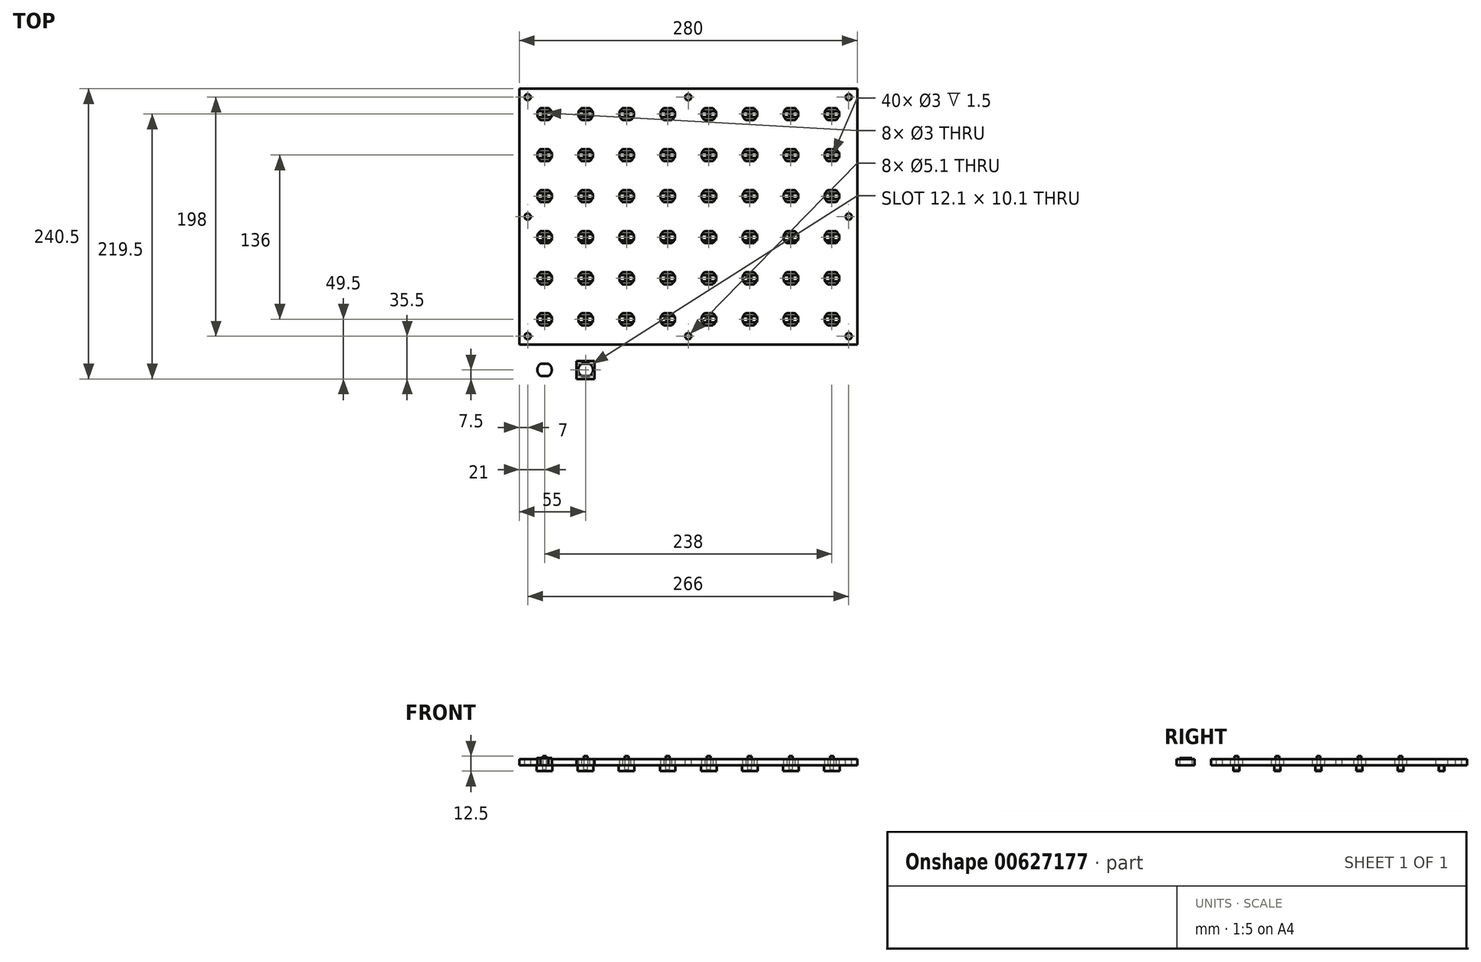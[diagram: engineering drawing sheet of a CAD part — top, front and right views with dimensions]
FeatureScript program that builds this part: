
annotation { "Feature Type Name" : "Feature", "Feature Type Description" : "" }
export const myFeature = defineFeature(function(context is Context, id is Id, definition is map)
    precondition{}
    {
        {
            var Q0;
            Q0=qCreatedBy(makeId("Top.planeOp"),FACE);
            var sketch = newSketch(context, id + "F0", { "sketchPlane" : qUnion([Q0])});
            skLineSegment(sketch, "E0.bottom", {"start": v(-140, -106) * mm, "end": v(140, -106) * mm});
            skLineSegment(sketch, "E0.top", {"start": v(-140, 106) * mm, "end": v(140, 106) * mm});
            skLineSegment(sketch, "E0.left", {"start": v(-140, -106) * mm, "end": v(-140, 106) * mm});
            skLineSegment(sketch, "E0.right", {"start": v(140, -106) * mm, "end": v(140, 106) * mm});
            skPoint(sketch, "E0.middle", {"position": v(0, 0) * mm});
            skLineSegment(sketch, "E1", {"start": v(-102, 141.86) * mm, "end": v(-102, -178.14) * mm, "construction": true});
            skLineSegment(sketch, "E2", {"start": v(-122.32, -80) * mm, "end": v(-115.68, -80) * mm});
            skLineSegment(sketch, "E3", {"start": v(-122.32, -90) * mm, "end": v(-115.68, -90) * mm});
            skArc(sketch, "E4", {"start": v(-122.32, -80) * mm, "mid": v(-125, -85) * mm, "end": v(-122.32, -90) * mm});
            skArc(sketch, "E5", {"start": v(-115.68, -90) * mm, "mid": v(-113, -85) * mm, "end": v(-115.68, -80) * mm});
            skLineSegment(sketch, "E6", {"start": v(-165.76, -85) * mm, "end": v(184.24, -85) * mm, "construction": true});
            skLineSegment(sketch, "E7.0.1.0", {"start": v(-165.76, -51) * mm, "end": v(184.24, -51) * mm, "construction": true});
            skArc(sketch, "E7.0.1.1", {"start": v(-122.32, -46) * mm, "mid": v(-125, -51) * mm, "end": v(-122.32, -56) * mm});
            skLineSegment(sketch, "E7.0.1.2", {"start": v(-122.32, -56) * mm, "end": v(-115.68, -56) * mm});
            skLineSegment(sketch, "E7.0.1.3", {"start": v(-122.32, -46) * mm, "end": v(-115.68, -46) * mm});
            skArc(sketch, "E7.0.1.4", {"start": v(-115.68, -56) * mm, "mid": v(-113, -51) * mm, "end": v(-115.68, -46) * mm});
            skLineSegment(sketch, "E7.0.2.0", {"start": v(-165.76, -17) * mm, "end": v(184.24, -17) * mm, "construction": true});
            skArc(sketch, "E7.0.2.1", {"start": v(-122.32, -12) * mm, "mid": v(-125, -17) * mm, "end": v(-122.32, -22) * mm});
            skLineSegment(sketch, "E7.0.2.2", {"start": v(-122.32, -22) * mm, "end": v(-115.68, -22) * mm});
            skLineSegment(sketch, "E7.0.2.3", {"start": v(-122.32, -12) * mm, "end": v(-115.68, -12) * mm});
            skArc(sketch, "E7.0.2.4", {"start": v(-115.68, -22) * mm, "mid": v(-113, -17) * mm, "end": v(-115.68, -12) * mm});
            skLineSegment(sketch, "E7.0.3.0", {"start": v(-165.76, 17) * mm, "end": v(184.24, 17) * mm, "construction": true});
            skArc(sketch, "E7.0.3.1", {"start": v(-122.32, 22) * mm, "mid": v(-125, 17) * mm, "end": v(-122.32, 12) * mm});
            skLineSegment(sketch, "E7.0.3.2", {"start": v(-122.32, 12) * mm, "end": v(-115.68, 12) * mm});
            skLineSegment(sketch, "E7.0.3.3", {"start": v(-122.32, 22) * mm, "end": v(-115.68, 22) * mm});
            skArc(sketch, "E7.0.3.4", {"start": v(-115.68, 12) * mm, "mid": v(-113, 17) * mm, "end": v(-115.68, 22) * mm});
            skLineSegment(sketch, "E7.0.4.0", {"start": v(-165.76, 51) * mm, "end": v(184.24, 51) * mm, "construction": true});
            skArc(sketch, "E7.0.4.1", {"start": v(-122.32, 56) * mm, "mid": v(-125, 51) * mm, "end": v(-122.32, 46) * mm});
            skLineSegment(sketch, "E7.0.4.2", {"start": v(-122.32, 46) * mm, "end": v(-115.68, 46) * mm});
            skLineSegment(sketch, "E7.0.4.3", {"start": v(-122.32, 56) * mm, "end": v(-115.68, 56) * mm});
            skArc(sketch, "E7.0.4.4", {"start": v(-115.68, 46) * mm, "mid": v(-113, 51) * mm, "end": v(-115.68, 56) * mm});
            skLineSegment(sketch, "E7.1.0.0", {"start": v(-131.76, -85) * mm, "end": v(218.24, -85) * mm, "construction": true});
            skArc(sketch, "E7.1.0.1", {"start": v(-88.32, -80) * mm, "mid": v(-91, -85) * mm, "end": v(-88.32, -90) * mm});
            skLineSegment(sketch, "E7.1.0.2", {"start": v(-88.32, -90) * mm, "end": v(-81.68, -90) * mm});
            skLineSegment(sketch, "E7.1.0.3", {"start": v(-88.32, -80) * mm, "end": v(-81.68, -80) * mm});
            skArc(sketch, "E7.1.0.4", {"start": v(-81.68, -90) * mm, "mid": v(-79, -85) * mm, "end": v(-81.68, -80) * mm});
            skLineSegment(sketch, "E7.1.1.0", {"start": v(-131.76, -51) * mm, "end": v(218.24, -51) * mm, "construction": true});
            skArc(sketch, "E7.1.1.1", {"start": v(-88.32, -46) * mm, "mid": v(-91, -51) * mm, "end": v(-88.32, -56) * mm});
            skLineSegment(sketch, "E7.1.1.2", {"start": v(-88.32, -56) * mm, "end": v(-81.68, -56) * mm});
            skLineSegment(sketch, "E7.1.1.3", {"start": v(-88.32, -46) * mm, "end": v(-81.68, -46) * mm});
            skArc(sketch, "E7.1.1.4", {"start": v(-81.68, -56) * mm, "mid": v(-79, -51) * mm, "end": v(-81.68, -46) * mm});
            skLineSegment(sketch, "E7.1.2.0", {"start": v(-131.76, -17) * mm, "end": v(218.24, -17) * mm, "construction": true});
            skArc(sketch, "E7.1.2.1", {"start": v(-88.32, -12) * mm, "mid": v(-91, -17) * mm, "end": v(-88.32, -22) * mm});
            skLineSegment(sketch, "E7.1.2.2", {"start": v(-88.32, -22) * mm, "end": v(-81.68, -22) * mm});
            skLineSegment(sketch, "E7.1.2.3", {"start": v(-88.32, -12) * mm, "end": v(-81.68, -12) * mm});
            skArc(sketch, "E7.1.2.4", {"start": v(-81.68, -22) * mm, "mid": v(-79, -17) * mm, "end": v(-81.68, -12) * mm});
            skLineSegment(sketch, "E7.1.3.0", {"start": v(-131.76, 17) * mm, "end": v(218.24, 17) * mm, "construction": true});
            skArc(sketch, "E7.1.3.1", {"start": v(-88.32, 22) * mm, "mid": v(-91, 17) * mm, "end": v(-88.32, 12) * mm});
            skLineSegment(sketch, "E7.1.3.2", {"start": v(-88.32, 12) * mm, "end": v(-81.68, 12) * mm});
            skLineSegment(sketch, "E7.1.3.3", {"start": v(-88.32, 22) * mm, "end": v(-81.68, 22) * mm});
            skArc(sketch, "E7.1.3.4", {"start": v(-81.68, 12) * mm, "mid": v(-79, 17) * mm, "end": v(-81.68, 22) * mm});
            skLineSegment(sketch, "E7.1.4.0", {"start": v(-131.76, 51) * mm, "end": v(218.24, 51) * mm, "construction": true});
            skArc(sketch, "E7.1.4.1", {"start": v(-88.32, 56) * mm, "mid": v(-91, 51) * mm, "end": v(-88.32, 46) * mm});
            skLineSegment(sketch, "E7.1.4.2", {"start": v(-88.32, 46) * mm, "end": v(-81.68, 46) * mm});
            skLineSegment(sketch, "E7.1.4.3", {"start": v(-88.32, 56) * mm, "end": v(-81.68, 56) * mm});
            skArc(sketch, "E7.1.4.4", {"start": v(-81.68, 46) * mm, "mid": v(-79, 51) * mm, "end": v(-81.68, 56) * mm});
            skLineSegment(sketch, "E7.2.0.0", {"start": v(-97.76, -85) * mm, "end": v(252.24, -85) * mm, "construction": true});
            skArc(sketch, "E7.2.0.1", {"start": v(-54.32, -80) * mm, "mid": v(-57, -85) * mm, "end": v(-54.32, -90) * mm});
            skLineSegment(sketch, "E7.2.0.2", {"start": v(-54.32, -90) * mm, "end": v(-47.68, -90) * mm});
            skLineSegment(sketch, "E7.2.0.3", {"start": v(-54.32, -80) * mm, "end": v(-47.68, -80) * mm});
            skArc(sketch, "E7.2.0.4", {"start": v(-47.68, -90) * mm, "mid": v(-45, -85) * mm, "end": v(-47.68, -80) * mm});
            skLineSegment(sketch, "E7.2.1.0", {"start": v(-97.76, -51) * mm, "end": v(252.24, -51) * mm, "construction": true});
            skArc(sketch, "E7.2.1.1", {"start": v(-54.32, -46) * mm, "mid": v(-57, -51) * mm, "end": v(-54.32, -56) * mm});
            skLineSegment(sketch, "E7.2.1.2", {"start": v(-54.32, -56) * mm, "end": v(-47.68, -56) * mm});
            skLineSegment(sketch, "E7.2.1.3", {"start": v(-54.32, -46) * mm, "end": v(-47.68, -46) * mm});
            skArc(sketch, "E7.2.1.4", {"start": v(-47.68, -56) * mm, "mid": v(-45, -51) * mm, "end": v(-47.68, -46) * mm});
            skLineSegment(sketch, "E7.2.2.0", {"start": v(-97.76, -17) * mm, "end": v(252.24, -17) * mm, "construction": true});
            skArc(sketch, "E7.2.2.1", {"start": v(-54.32, -12) * mm, "mid": v(-57, -17) * mm, "end": v(-54.32, -22) * mm});
            skLineSegment(sketch, "E7.2.2.2", {"start": v(-54.32, -22) * mm, "end": v(-47.68, -22) * mm});
            skLineSegment(sketch, "E7.2.2.3", {"start": v(-54.32, -12) * mm, "end": v(-47.68, -12) * mm});
            skArc(sketch, "E7.2.2.4", {"start": v(-47.68, -22) * mm, "mid": v(-45, -17) * mm, "end": v(-47.68, -12) * mm});
            skLineSegment(sketch, "E7.2.3.0", {"start": v(-97.76, 17) * mm, "end": v(252.24, 17) * mm, "construction": true});
            skArc(sketch, "E7.2.3.1", {"start": v(-54.32, 22) * mm, "mid": v(-57, 17) * mm, "end": v(-54.32, 12) * mm});
            skLineSegment(sketch, "E7.2.3.2", {"start": v(-54.32, 12) * mm, "end": v(-47.68, 12) * mm});
            skLineSegment(sketch, "E7.2.3.3", {"start": v(-54.32, 22) * mm, "end": v(-47.68, 22) * mm});
            skArc(sketch, "E7.2.3.4", {"start": v(-47.68, 12) * mm, "mid": v(-45, 17) * mm, "end": v(-47.68, 22) * mm});
            skLineSegment(sketch, "E7.2.4.0", {"start": v(-97.76, 51) * mm, "end": v(252.24, 51) * mm, "construction": true});
            skArc(sketch, "E7.2.4.1", {"start": v(-54.32, 56) * mm, "mid": v(-57, 51) * mm, "end": v(-54.32, 46) * mm});
            skLineSegment(sketch, "E7.2.4.2", {"start": v(-54.32, 46) * mm, "end": v(-47.68, 46) * mm});
            skLineSegment(sketch, "E7.2.4.3", {"start": v(-54.32, 56) * mm, "end": v(-47.68, 56) * mm});
            skArc(sketch, "E7.2.4.4", {"start": v(-47.68, 46) * mm, "mid": v(-45, 51) * mm, "end": v(-47.68, 56) * mm});
            skLineSegment(sketch, "E7.3.0.0", {"start": v(-63.76, -85) * mm, "end": v(286.24, -85) * mm, "construction": true});
            skArc(sketch, "E7.3.0.1", {"start": v(-20.32, -80) * mm, "mid": v(-23, -85) * mm, "end": v(-20.32, -90) * mm});
            skLineSegment(sketch, "E7.3.0.2", {"start": v(-20.32, -90) * mm, "end": v(-13.68, -90) * mm});
            skLineSegment(sketch, "E7.3.0.3", {"start": v(-20.32, -80) * mm, "end": v(-13.68, -80) * mm});
            skArc(sketch, "E7.3.0.4", {"start": v(-13.68, -90) * mm, "mid": v(-11, -85) * mm, "end": v(-13.68, -80) * mm});
            skLineSegment(sketch, "E7.3.1.0", {"start": v(-63.76, -51) * mm, "end": v(286.24, -51) * mm, "construction": true});
            skArc(sketch, "E7.3.1.1", {"start": v(-20.32, -46) * mm, "mid": v(-23, -51) * mm, "end": v(-20.32, -56) * mm});
            skLineSegment(sketch, "E7.3.1.2", {"start": v(-20.32, -56) * mm, "end": v(-13.68, -56) * mm});
            skLineSegment(sketch, "E7.3.1.3", {"start": v(-20.32, -46) * mm, "end": v(-13.68, -46) * mm});
            skArc(sketch, "E7.3.1.4", {"start": v(-13.68, -56) * mm, "mid": v(-11, -51) * mm, "end": v(-13.68, -46) * mm});
            skLineSegment(sketch, "E7.3.2.0", {"start": v(-63.76, -17) * mm, "end": v(286.24, -17) * mm, "construction": true});
            skArc(sketch, "E7.3.2.1", {"start": v(-20.32, -12) * mm, "mid": v(-23, -17) * mm, "end": v(-20.32, -22) * mm});
            skLineSegment(sketch, "E7.3.2.2", {"start": v(-20.32, -22) * mm, "end": v(-13.68, -22) * mm});
            skLineSegment(sketch, "E7.3.2.3", {"start": v(-20.32, -12) * mm, "end": v(-13.68, -12) * mm});
            skArc(sketch, "E7.3.2.4", {"start": v(-13.68, -22) * mm, "mid": v(-11, -17) * mm, "end": v(-13.68, -12) * mm});
            skLineSegment(sketch, "E7.3.3.0", {"start": v(-63.76, 17) * mm, "end": v(286.24, 17) * mm, "construction": true});
            skArc(sketch, "E7.3.3.1", {"start": v(-20.32, 22) * mm, "mid": v(-23, 17) * mm, "end": v(-20.32, 12) * mm});
            skLineSegment(sketch, "E7.3.3.2", {"start": v(-20.32, 12) * mm, "end": v(-13.68, 12) * mm});
            skLineSegment(sketch, "E7.3.3.3", {"start": v(-20.32, 22) * mm, "end": v(-13.68, 22) * mm});
            skArc(sketch, "E7.3.3.4", {"start": v(-13.68, 12) * mm, "mid": v(-11, 17) * mm, "end": v(-13.68, 22) * mm});
            skLineSegment(sketch, "E7.3.4.0", {"start": v(-63.76, 51) * mm, "end": v(286.24, 51) * mm, "construction": true});
            skArc(sketch, "E7.3.4.1", {"start": v(-20.32, 56) * mm, "mid": v(-23, 51) * mm, "end": v(-20.32, 46) * mm});
            skLineSegment(sketch, "E7.3.4.2", {"start": v(-20.32, 46) * mm, "end": v(-13.68, 46) * mm});
            skLineSegment(sketch, "E7.3.4.3", {"start": v(-20.32, 56) * mm, "end": v(-13.68, 56) * mm});
            skArc(sketch, "E7.3.4.4", {"start": v(-13.68, 46) * mm, "mid": v(-11, 51) * mm, "end": v(-13.68, 56) * mm});
            skLineSegment(sketch, "E7.4.0.0", {"start": v(-29.76, -85) * mm, "end": v(320.24, -85) * mm, "construction": true});
            skArc(sketch, "E7.4.0.1", {"start": v(13.68, -80) * mm, "mid": v(11, -85) * mm, "end": v(13.68, -90) * mm});
            skLineSegment(sketch, "E7.4.0.2", {"start": v(13.68, -90) * mm, "end": v(20.32, -90) * mm});
            skLineSegment(sketch, "E7.4.0.3", {"start": v(13.68, -80) * mm, "end": v(20.32, -80) * mm});
            skArc(sketch, "E7.4.0.4", {"start": v(20.32, -90) * mm, "mid": v(23, -85) * mm, "end": v(20.32, -80) * mm});
            skLineSegment(sketch, "E7.4.1.0", {"start": v(-29.76, -51) * mm, "end": v(320.24, -51) * mm, "construction": true});
            skArc(sketch, "E7.4.1.1", {"start": v(13.68, -46) * mm, "mid": v(11, -51) * mm, "end": v(13.68, -56) * mm});
            skLineSegment(sketch, "E7.4.1.2", {"start": v(13.68, -56) * mm, "end": v(20.32, -56) * mm});
            skLineSegment(sketch, "E7.4.1.3", {"start": v(13.68, -46) * mm, "end": v(20.32, -46) * mm});
            skArc(sketch, "E7.4.1.4", {"start": v(20.32, -56) * mm, "mid": v(23, -51) * mm, "end": v(20.32, -46) * mm});
            skLineSegment(sketch, "E7.4.2.0", {"start": v(-29.76, -17) * mm, "end": v(320.24, -17) * mm, "construction": true});
            skArc(sketch, "E7.4.2.1", {"start": v(13.68, -12) * mm, "mid": v(11, -17) * mm, "end": v(13.68, -22) * mm});
            skLineSegment(sketch, "E7.4.2.2", {"start": v(13.68, -22) * mm, "end": v(20.32, -22) * mm});
            skLineSegment(sketch, "E7.4.2.3", {"start": v(13.68, -12) * mm, "end": v(20.32, -12) * mm});
            skArc(sketch, "E7.4.2.4", {"start": v(20.32, -22) * mm, "mid": v(23, -17) * mm, "end": v(20.32, -12) * mm});
            skLineSegment(sketch, "E7.4.3.0", {"start": v(-29.76, 17) * mm, "end": v(320.24, 17) * mm, "construction": true});
            skArc(sketch, "E7.4.3.1", {"start": v(13.68, 22) * mm, "mid": v(11, 17) * mm, "end": v(13.68, 12) * mm});
            skLineSegment(sketch, "E7.4.3.2", {"start": v(13.68, 12) * mm, "end": v(20.32, 12) * mm});
            skLineSegment(sketch, "E7.4.3.3", {"start": v(13.68, 22) * mm, "end": v(20.32, 22) * mm});
            skArc(sketch, "E7.4.3.4", {"start": v(20.32, 12) * mm, "mid": v(23, 17) * mm, "end": v(20.32, 22) * mm});
            skLineSegment(sketch, "E7.4.4.0", {"start": v(-29.76, 51) * mm, "end": v(320.24, 51) * mm, "construction": true});
            skArc(sketch, "E7.4.4.1", {"start": v(13.68, 56) * mm, "mid": v(11, 51) * mm, "end": v(13.68, 46) * mm});
            skLineSegment(sketch, "E7.4.4.2", {"start": v(13.68, 46) * mm, "end": v(20.32, 46) * mm});
            skLineSegment(sketch, "E7.4.4.3", {"start": v(13.68, 56) * mm, "end": v(20.32, 56) * mm});
            skArc(sketch, "E7.4.4.4", {"start": v(20.32, 46) * mm, "mid": v(23, 51) * mm, "end": v(20.32, 56) * mm});
            skLineSegment(sketch, "E7.5.0.0", {"start": v(4.24, -85) * mm, "end": v(354.24, -85) * mm, "construction": true});
            skArc(sketch, "E7.5.0.1", {"start": v(47.68, -80) * mm, "mid": v(45, -85) * mm, "end": v(47.68, -90) * mm});
            skLineSegment(sketch, "E7.5.0.2", {"start": v(47.68, -90) * mm, "end": v(54.32, -90) * mm});
            skLineSegment(sketch, "E7.5.0.3", {"start": v(47.68, -80) * mm, "end": v(54.32, -80) * mm});
            skArc(sketch, "E7.5.0.4", {"start": v(54.32, -90) * mm, "mid": v(57, -85) * mm, "end": v(54.32, -80) * mm});
            skLineSegment(sketch, "E7.5.1.0", {"start": v(4.24, -51) * mm, "end": v(354.24, -51) * mm, "construction": true});
            skArc(sketch, "E7.5.1.1", {"start": v(47.68, -46) * mm, "mid": v(45, -51) * mm, "end": v(47.68, -56) * mm});
            skLineSegment(sketch, "E7.5.1.2", {"start": v(47.68, -56) * mm, "end": v(54.32, -56) * mm});
            skLineSegment(sketch, "E7.5.1.3", {"start": v(47.68, -46) * mm, "end": v(54.32, -46) * mm});
            skArc(sketch, "E7.5.1.4", {"start": v(54.32, -56) * mm, "mid": v(57, -51) * mm, "end": v(54.32, -46) * mm});
            skLineSegment(sketch, "E7.5.2.0", {"start": v(4.24, -17) * mm, "end": v(354.24, -17) * mm, "construction": true});
            skArc(sketch, "E7.5.2.1", {"start": v(47.68, -12) * mm, "mid": v(45, -17) * mm, "end": v(47.68, -22) * mm});
            skLineSegment(sketch, "E7.5.2.2", {"start": v(47.68, -22) * mm, "end": v(54.32, -22) * mm});
            skLineSegment(sketch, "E7.5.2.3", {"start": v(47.68, -12) * mm, "end": v(54.32, -12) * mm});
            skArc(sketch, "E7.5.2.4", {"start": v(54.32, -22) * mm, "mid": v(57, -17) * mm, "end": v(54.32, -12) * mm});
            skLineSegment(sketch, "E7.5.3.0", {"start": v(4.24, 17) * mm, "end": v(354.24, 17) * mm, "construction": true});
            skArc(sketch, "E7.5.3.1", {"start": v(47.68, 22) * mm, "mid": v(45, 17) * mm, "end": v(47.68, 12) * mm});
            skLineSegment(sketch, "E7.5.3.2", {"start": v(47.68, 12) * mm, "end": v(54.32, 12) * mm});
            skLineSegment(sketch, "E7.5.3.3", {"start": v(47.68, 22) * mm, "end": v(54.32, 22) * mm});
            skArc(sketch, "E7.5.3.4", {"start": v(54.32, 12) * mm, "mid": v(57, 17) * mm, "end": v(54.32, 22) * mm});
            skLineSegment(sketch, "E7.5.4.0", {"start": v(4.24, 51) * mm, "end": v(354.24, 51) * mm, "construction": true});
            skArc(sketch, "E7.5.4.1", {"start": v(47.68, 56) * mm, "mid": v(45, 51) * mm, "end": v(47.68, 46) * mm});
            skLineSegment(sketch, "E7.5.4.2", {"start": v(47.68, 46) * mm, "end": v(54.32, 46) * mm});
            skLineSegment(sketch, "E7.5.4.3", {"start": v(47.68, 56) * mm, "end": v(54.32, 56) * mm});
            skArc(sketch, "E7.5.4.4", {"start": v(54.32, 46) * mm, "mid": v(57, 51) * mm, "end": v(54.32, 56) * mm});
            skLineSegment(sketch, "E7.6.0.0", {"start": v(38.24, -85) * mm, "end": v(388.24, -85) * mm, "construction": true});
            skArc(sketch, "E7.6.0.1", {"start": v(81.68, -80) * mm, "mid": v(79, -85) * mm, "end": v(81.68, -90) * mm});
            skLineSegment(sketch, "E7.6.0.2", {"start": v(81.68, -90) * mm, "end": v(88.32, -90) * mm});
            skLineSegment(sketch, "E7.6.0.3", {"start": v(81.68, -80) * mm, "end": v(88.32, -80) * mm});
            skArc(sketch, "E7.6.0.4", {"start": v(88.32, -90) * mm, "mid": v(91, -85) * mm, "end": v(88.32, -80) * mm});
            skLineSegment(sketch, "E7.6.1.0", {"start": v(38.24, -51) * mm, "end": v(388.24, -51) * mm, "construction": true});
            skArc(sketch, "E7.6.1.1", {"start": v(81.68, -46) * mm, "mid": v(79, -51) * mm, "end": v(81.68, -56) * mm});
            skLineSegment(sketch, "E7.6.1.2", {"start": v(81.68, -56) * mm, "end": v(88.32, -56) * mm});
            skLineSegment(sketch, "E7.6.1.3", {"start": v(81.68, -46) * mm, "end": v(88.32, -46) * mm});
            skArc(sketch, "E7.6.1.4", {"start": v(88.32, -56) * mm, "mid": v(91, -51) * mm, "end": v(88.32, -46) * mm});
            skLineSegment(sketch, "E7.6.2.0", {"start": v(38.24, -17) * mm, "end": v(388.24, -17) * mm, "construction": true});
            skArc(sketch, "E7.6.2.1", {"start": v(81.68, -12) * mm, "mid": v(79, -17) * mm, "end": v(81.68, -22) * mm});
            skLineSegment(sketch, "E7.6.2.2", {"start": v(81.68, -22) * mm, "end": v(88.32, -22) * mm});
            skLineSegment(sketch, "E7.6.2.3", {"start": v(81.68, -12) * mm, "end": v(88.32, -12) * mm});
            skArc(sketch, "E7.6.2.4", {"start": v(88.32, -22) * mm, "mid": v(91, -17) * mm, "end": v(88.32, -12) * mm});
            skLineSegment(sketch, "E7.6.3.0", {"start": v(38.24, 17) * mm, "end": v(388.24, 17) * mm, "construction": true});
            skArc(sketch, "E7.6.3.1", {"start": v(81.68, 22) * mm, "mid": v(79, 17) * mm, "end": v(81.68, 12) * mm});
            skLineSegment(sketch, "E7.6.3.2", {"start": v(81.68, 12) * mm, "end": v(88.32, 12) * mm});
            skLineSegment(sketch, "E7.6.3.3", {"start": v(81.68, 22) * mm, "end": v(88.32, 22) * mm});
            skArc(sketch, "E7.6.3.4", {"start": v(88.32, 12) * mm, "mid": v(91, 17) * mm, "end": v(88.32, 22) * mm});
            skLineSegment(sketch, "E7.6.4.0", {"start": v(38.24, 51) * mm, "end": v(388.24, 51) * mm, "construction": true});
            skArc(sketch, "E7.6.4.1", {"start": v(81.68, 56) * mm, "mid": v(79, 51) * mm, "end": v(81.68, 46) * mm});
            skLineSegment(sketch, "E7.6.4.2", {"start": v(81.68, 46) * mm, "end": v(88.32, 46) * mm});
            skLineSegment(sketch, "E7.6.4.3", {"start": v(81.68, 56) * mm, "end": v(88.32, 56) * mm});
            skArc(sketch, "E7.6.4.4", {"start": v(88.32, 46) * mm, "mid": v(91, 51) * mm, "end": v(88.32, 56) * mm});
            skArc(sketch, "E7.7.0.1", {"start": v(115.68, -80) * mm, "mid": v(113, -85) * mm, "end": v(115.68, -90) * mm});
            skLineSegment(sketch, "E7.7.0.2", {"start": v(115.68, -90) * mm, "end": v(122.32, -90) * mm});
            skLineSegment(sketch, "E7.7.0.3", {"start": v(115.68, -80) * mm, "end": v(122.32, -80) * mm});
            skArc(sketch, "E7.7.0.4", {"start": v(122.32, -90) * mm, "mid": v(125, -85) * mm, "end": v(122.32, -80) * mm});
            skArc(sketch, "E7.7.1.1", {"start": v(115.68, -46) * mm, "mid": v(113, -51) * mm, "end": v(115.68, -56) * mm});
            skLineSegment(sketch, "E7.7.1.2", {"start": v(115.68, -56) * mm, "end": v(122.32, -56) * mm});
            skLineSegment(sketch, "E7.7.1.3", {"start": v(115.68, -46) * mm, "end": v(122.32, -46) * mm});
            skArc(sketch, "E7.7.1.4", {"start": v(122.32, -56) * mm, "mid": v(125, -51) * mm, "end": v(122.32, -46) * mm});
            skArc(sketch, "E7.7.2.1", {"start": v(115.68, -12) * mm, "mid": v(113, -17) * mm, "end": v(115.68, -22) * mm});
            skLineSegment(sketch, "E7.7.2.2", {"start": v(115.68, -22) * mm, "end": v(122.32, -22) * mm});
            skLineSegment(sketch, "E7.7.2.3", {"start": v(115.68, -12) * mm, "end": v(122.32, -12) * mm});
            skArc(sketch, "E7.7.2.4", {"start": v(122.32, -22) * mm, "mid": v(125, -17) * mm, "end": v(122.32, -12) * mm});
            skArc(sketch, "E7.7.3.1", {"start": v(115.68, 22) * mm, "mid": v(113, 17) * mm, "end": v(115.68, 12) * mm});
            skLineSegment(sketch, "E7.7.3.2", {"start": v(115.68, 12) * mm, "end": v(122.32, 12) * mm});
            skLineSegment(sketch, "E7.7.3.3", {"start": v(115.68, 22) * mm, "end": v(122.32, 22) * mm});
            skArc(sketch, "E7.7.3.4", {"start": v(122.32, 12) * mm, "mid": v(125, 17) * mm, "end": v(122.32, 22) * mm});
            skArc(sketch, "E7.7.4.1", {"start": v(115.68, 56) * mm, "mid": v(113, 51) * mm, "end": v(115.68, 46) * mm});
            skLineSegment(sketch, "E7.7.4.2", {"start": v(115.68, 46) * mm, "end": v(122.32, 46) * mm});
            skLineSegment(sketch, "E7.7.4.3", {"start": v(115.68, 56) * mm, "end": v(122.32, 56) * mm});
            skArc(sketch, "E7.7.4.4", {"start": v(122.32, 46) * mm, "mid": v(125, 51) * mm, "end": v(122.32, 56) * mm});
            skLineSegment(sketch, "E7.direction1", {"start": v(-165.76, -85) * mm, "end": v(-131.76, -85) * mm, "construction": true});
            skLineSegment(sketch, "E7.direction2", {"start": v(-165.76, -85) * mm, "end": v(-165.76, -51) * mm, "construction": true});
            skLineSegment(sketch, "E8.0.0.5", {"start": v(-165.76, 85) * mm, "end": v(184.24, 85) * mm, "construction": true});
            skArc(sketch, "E8.3.0.5", {"start": v(-122.32, 90) * mm, "mid": v(-125, 85) * mm, "end": v(-122.32, 80) * mm});
            skLineSegment(sketch, "E8.7.0.5", {"start": v(-122.32, 80) * mm, "end": v(-115.68, 80) * mm});
            skLineSegment(sketch, "E8.10.0.5", {"start": v(-122.32, 90) * mm, "end": v(-115.68, 90) * mm});
            skArc(sketch, "E8.13.0.5", {"start": v(-115.68, 80) * mm, "mid": v(-113, 85) * mm, "end": v(-115.68, 90) * mm});
            skLineSegment(sketch, "E8.0.1.5", {"start": v(-131.76, 85) * mm, "end": v(218.24, 85) * mm, "construction": true});
            skArc(sketch, "E8.3.1.5", {"start": v(-88.32, 90) * mm, "mid": v(-91, 85) * mm, "end": v(-88.32, 80) * mm});
            skLineSegment(sketch, "E8.7.1.5", {"start": v(-88.32, 80) * mm, "end": v(-81.68, 80) * mm});
            skLineSegment(sketch, "E8.10.1.5", {"start": v(-88.32, 90) * mm, "end": v(-81.68, 90) * mm});
            skArc(sketch, "E8.13.1.5", {"start": v(-81.68, 80) * mm, "mid": v(-79, 85) * mm, "end": v(-81.68, 90) * mm});
            skLineSegment(sketch, "E8.0.2.5", {"start": v(-97.76, 85) * mm, "end": v(252.24, 85) * mm, "construction": true});
            skArc(sketch, "E8.3.2.5", {"start": v(-54.32, 90) * mm, "mid": v(-57, 85) * mm, "end": v(-54.32, 80) * mm});
            skLineSegment(sketch, "E8.7.2.5", {"start": v(-54.32, 80) * mm, "end": v(-47.68, 80) * mm});
            skLineSegment(sketch, "E8.10.2.5", {"start": v(-54.32, 90) * mm, "end": v(-47.68, 90) * mm});
            skArc(sketch, "E8.13.2.5", {"start": v(-47.68, 80) * mm, "mid": v(-45, 85) * mm, "end": v(-47.68, 90) * mm});
            skLineSegment(sketch, "E8.0.3.5", {"start": v(-63.76, 85) * mm, "end": v(286.24, 85) * mm, "construction": true});
            skArc(sketch, "E8.3.3.5", {"start": v(-20.32, 90) * mm, "mid": v(-23, 85) * mm, "end": v(-20.32, 80) * mm});
            skLineSegment(sketch, "E8.7.3.5", {"start": v(-20.32, 80) * mm, "end": v(-13.68, 80) * mm});
            skLineSegment(sketch, "E8.10.3.5", {"start": v(-20.32, 90) * mm, "end": v(-13.68, 90) * mm});
            skArc(sketch, "E8.13.3.5", {"start": v(-13.68, 80) * mm, "mid": v(-11, 85) * mm, "end": v(-13.68, 90) * mm});
            skLineSegment(sketch, "E8.0.4.5", {"start": v(-29.76, 85) * mm, "end": v(320.24, 85) * mm, "construction": true});
            skArc(sketch, "E8.3.4.5", {"start": v(13.68, 90) * mm, "mid": v(11, 85) * mm, "end": v(13.68, 80) * mm});
            skLineSegment(sketch, "E8.7.4.5", {"start": v(13.68, 80) * mm, "end": v(20.32, 80) * mm});
            skLineSegment(sketch, "E8.10.4.5", {"start": v(13.68, 90) * mm, "end": v(20.32, 90) * mm});
            skArc(sketch, "E8.13.4.5", {"start": v(20.32, 80) * mm, "mid": v(23, 85) * mm, "end": v(20.32, 90) * mm});
            skLineSegment(sketch, "E8.0.5.5", {"start": v(4.24, 85) * mm, "end": v(354.24, 85) * mm, "construction": true});
            skArc(sketch, "E8.3.5.5", {"start": v(47.68, 90) * mm, "mid": v(45, 85) * mm, "end": v(47.68, 80) * mm});
            skLineSegment(sketch, "E8.7.5.5", {"start": v(47.68, 80) * mm, "end": v(54.32, 80) * mm});
            skLineSegment(sketch, "E8.10.5.5", {"start": v(47.68, 90) * mm, "end": v(54.32, 90) * mm});
            skArc(sketch, "E8.13.5.5", {"start": v(54.32, 80) * mm, "mid": v(57, 85) * mm, "end": v(54.32, 90) * mm});
            skLineSegment(sketch, "E8.0.6.5", {"start": v(38.24, 85) * mm, "end": v(388.24, 85) * mm, "construction": true});
            skArc(sketch, "E8.3.6.5", {"start": v(81.68, 90) * mm, "mid": v(79, 85) * mm, "end": v(81.68, 80) * mm});
            skLineSegment(sketch, "E8.7.6.5", {"start": v(81.68, 80) * mm, "end": v(88.32, 80) * mm});
            skLineSegment(sketch, "E8.10.6.5", {"start": v(81.68, 90) * mm, "end": v(88.32, 90) * mm});
            skArc(sketch, "E8.13.6.5", {"start": v(88.32, 80) * mm, "mid": v(91, 85) * mm, "end": v(88.32, 90) * mm});
            skLineSegment(sketch, "E8.0.7.5", {"start": v(72.24, 85) * mm, "end": v(422.24, 85) * mm, "construction": true});
            skArc(sketch, "E8.3.7.5", {"start": v(115.68, 90) * mm, "mid": v(113, 85) * mm, "end": v(115.68, 80) * mm});
            skLineSegment(sketch, "E8.7.7.5", {"start": v(115.68, 80) * mm, "end": v(122.32, 80) * mm});
            skLineSegment(sketch, "E8.10.7.5", {"start": v(115.68, 90) * mm, "end": v(122.32, 90) * mm});
            skArc(sketch, "E8.13.7.5", {"start": v(122.32, 80) * mm, "mid": v(125, 85) * mm, "end": v(122.32, 90) * mm});
            skArc(sketch, "E9.MirrorCS", {"start": v(-122.32, -132) * mm, "mid": v(-125, -127) * mm, "end": v(-122.32, -122) * mm});
            skLineSegment(sketch, "E10.MirrorCS", {"start": v(-122.32, -132) * mm, "end": v(-115.68, -132) * mm});
            skArc(sketch, "E11.MirrorCS", {"start": v(-115.68, -122) * mm, "mid": v(-113, -127) * mm, "end": v(-115.68, -132) * mm});
            skLineSegment(sketch, "E12.MirrorCS", {"start": v(-122.32, -122) * mm, "end": v(-115.68, -122) * mm});
            skLineSegment(sketch, "E13.bottom", {"start": v(-111.5, -134.5) * mm, "end": v(-126.5, -134.5) * mm});
            skLineSegment(sketch, "E13.top", {"start": v(-111.5, -119.5) * mm, "end": v(-126.5, -119.5) * mm});
            skLineSegment(sketch, "E13.left", {"start": v(-111.5, -134.5) * mm, "end": v(-111.5, -119.5) * mm});
            skLineSegment(sketch, "E13.right", {"start": v(-126.5, -134.5) * mm, "end": v(-126.5, -119.5) * mm});
            skLineSegment(sketch, "E14.MirrorCS", {"start": v(-92.5, -134.5) * mm, "end": v(-92.5, -119.5) * mm});
            skLineSegment(sketch, "E15.MirrorCS", {"start": v(-92.5, -119.5) * mm, "end": v(-77.5, -119.5) * mm});
            skLineSegment(sketch, "E16.MirrorCS", {"start": v(-77.5, -134.5) * mm, "end": v(-77.5, -119.5) * mm});
            skLineSegment(sketch, "E17.MirrorCS", {"start": v(-92.5, -134.5) * mm, "end": v(-77.5, -134.5) * mm});
            skCircle(sketch, "E18", {"center": v(-85, -127) * mm, "radius": 6.05 * mm});
            skPoint(sketch, "E18.centerSnap0", {"position": v(-85, -119.5) * mm});
            skPoint(sketch, "E18.centerSnap1", {"position": v(-77.5, -127) * mm});
            skLineSegment(sketch, "E19", {"start": v(-88.33, -121.95) * mm, "end": v(-81.67, -121.95) * mm});
            skLineSegment(sketch, "E20", {"start": v(-88.33, -132.05) * mm, "end": v(-81.67, -132.05) * mm});
            skSolve(sketch);
        }
        {
            var Q0;
            Q0=makeQuery(id+"F0.imprint","IMPRINT",FACE,{"disambiguationData":[TD([[makeQuery(id+"F0.imprint","IMPRINT",EDGE,{"derivedFrom":sQuery(id+"F0.wireOp",EDGE,"E0.bottom")}),1.0]])]});
            extrude(context, id + "F1", {"entities" : qUnion([Q0]), "depth" : 5 * mm, "offsetDistance" : 25 * mm});
        }
        {
            var Q0;
            Q0=makeQuery(id+"F1.opExtrude","CAP_FACE",FACE,{"disambiguationData":[OSD([sQuery(id+"F0.wireOp",EDGE,"E0.bottom"),sQuery(id+"F0.wireOp",EDGE,"E0.top"),sQuery(id+"F0.wireOp",EDGE,"E0.left"),sQuery(id+"F0.wireOp",EDGE,"E0.right"),sQuery(id+"F0.wireOp",EDGE,"E2"),sQuery(id+"F0.wireOp",EDGE,"E3"),sQuery(id+"F0.wireOp",EDGE,"E4"),sQuery(id+"F0.wireOp",EDGE,"E5"),sQuery(id+"F0.wireOp",EDGE,"E7.0.1.1"),sQuery(id+"F0.wireOp",EDGE,"E7.0.1.2"),sQuery(id+"F0.wireOp",EDGE,"E7.0.1.3"),sQuery(id+"F0.wireOp",EDGE,"E7.0.1.4"),sQuery(id+"F0.wireOp",EDGE,"E7.0.2.1"),sQuery(id+"F0.wireOp",EDGE,"E7.0.2.2"),sQuery(id+"F0.wireOp",EDGE,"E7.0.2.3"),sQuery(id+"F0.wireOp",EDGE,"E7.0.2.4"),sQuery(id+"F0.wireOp",EDGE,"E7.0.3.1"),sQuery(id+"F0.wireOp",EDGE,"E7.0.3.2"),sQuery(id+"F0.wireOp",EDGE,"E7.0.3.3"),sQuery(id+"F0.wireOp",EDGE,"E7.0.3.4"),sQuery(id+"F0.wireOp",EDGE,"E7.0.4.1"),sQuery(id+"F0.wireOp",EDGE,"E7.0.4.2"),sQuery(id+"F0.wireOp",EDGE,"E7.0.4.3"),sQuery(id+"F0.wireOp",EDGE,"E7.0.4.4"),sQuery(id+"F0.wireOp",EDGE,"E7.1.0.1"),sQuery(id+"F0.wireOp",EDGE,"E7.1.0.2"),sQuery(id+"F0.wireOp",EDGE,"E7.1.0.3"),sQuery(id+"F0.wireOp",EDGE,"E7.1.0.4"),sQuery(id+"F0.wireOp",EDGE,"E7.1.1.1"),sQuery(id+"F0.wireOp",EDGE,"E7.1.1.2"),sQuery(id+"F0.wireOp",EDGE,"E7.1.1.3"),sQuery(id+"F0.wireOp",EDGE,"E7.1.1.4"),sQuery(id+"F0.wireOp",EDGE,"E7.1.2.1"),sQuery(id+"F0.wireOp",EDGE,"E7.1.2.2"),sQuery(id+"F0.wireOp",EDGE,"E7.1.2.3"),sQuery(id+"F0.wireOp",EDGE,"E7.1.2.4"),sQuery(id+"F0.wireOp",EDGE,"E7.1.3.1"),sQuery(id+"F0.wireOp",EDGE,"E7.1.3.2"),sQuery(id+"F0.wireOp",EDGE,"E7.1.3.3"),sQuery(id+"F0.wireOp",EDGE,"E7.1.3.4"),sQuery(id+"F0.wireOp",EDGE,"E7.1.4.1"),sQuery(id+"F0.wireOp",EDGE,"E7.1.4.2"),sQuery(id+"F0.wireOp",EDGE,"E7.1.4.3"),sQuery(id+"F0.wireOp",EDGE,"E7.1.4.4"),sQuery(id+"F0.wireOp",EDGE,"E7.2.0.1"),sQuery(id+"F0.wireOp",EDGE,"E7.2.0.2"),sQuery(id+"F0.wireOp",EDGE,"E7.2.0.3"),sQuery(id+"F0.wireOp",EDGE,"E7.2.0.4"),sQuery(id+"F0.wireOp",EDGE,"E7.2.1.1"),sQuery(id+"F0.wireOp",EDGE,"E7.2.1.2"),sQuery(id+"F0.wireOp",EDGE,"E7.2.1.3"),sQuery(id+"F0.wireOp",EDGE,"E7.2.1.4"),sQuery(id+"F0.wireOp",EDGE,"E7.2.2.1"),sQuery(id+"F0.wireOp",EDGE,"E7.2.2.2"),sQuery(id+"F0.wireOp",EDGE,"E7.2.2.3"),sQuery(id+"F0.wireOp",EDGE,"E7.2.2.4"),sQuery(id+"F0.wireOp",EDGE,"E7.2.3.1"),sQuery(id+"F0.wireOp",EDGE,"E7.2.3.2"),sQuery(id+"F0.wireOp",EDGE,"E7.2.3.3"),sQuery(id+"F0.wireOp",EDGE,"E7.2.3.4"),sQuery(id+"F0.wireOp",EDGE,"E7.2.4.1"),sQuery(id+"F0.wireOp",EDGE,"E7.2.4.2"),sQuery(id+"F0.wireOp",EDGE,"E7.2.4.3"),sQuery(id+"F0.wireOp",EDGE,"E7.2.4.4"),sQuery(id+"F0.wireOp",EDGE,"E7.3.0.1"),sQuery(id+"F0.wireOp",EDGE,"E7.3.0.2"),sQuery(id+"F0.wireOp",EDGE,"E7.3.0.3"),sQuery(id+"F0.wireOp",EDGE,"E7.3.0.4"),sQuery(id+"F0.wireOp",EDGE,"E7.3.1.1"),sQuery(id+"F0.wireOp",EDGE,"E7.3.1.2"),sQuery(id+"F0.wireOp",EDGE,"E7.3.1.3"),sQuery(id+"F0.wireOp",EDGE,"E7.3.1.4"),sQuery(id+"F0.wireOp",EDGE,"E7.3.2.1"),sQuery(id+"F0.wireOp",EDGE,"E7.3.2.2"),sQuery(id+"F0.wireOp",EDGE,"E7.3.2.3"),sQuery(id+"F0.wireOp",EDGE,"E7.3.2.4"),sQuery(id+"F0.wireOp",EDGE,"E7.3.3.1"),sQuery(id+"F0.wireOp",EDGE,"E7.3.3.2"),sQuery(id+"F0.wireOp",EDGE,"E7.3.3.3"),sQuery(id+"F0.wireOp",EDGE,"E7.3.3.4"),sQuery(id+"F0.wireOp",EDGE,"E7.3.4.1"),sQuery(id+"F0.wireOp",EDGE,"E7.3.4.2"),sQuery(id+"F0.wireOp",EDGE,"E7.3.4.3"),sQuery(id+"F0.wireOp",EDGE,"E7.3.4.4"),sQuery(id+"F0.wireOp",EDGE,"E7.4.0.1"),sQuery(id+"F0.wireOp",EDGE,"E7.4.0.2"),sQuery(id+"F0.wireOp",EDGE,"E7.4.0.3"),sQuery(id+"F0.wireOp",EDGE,"E7.4.0.4"),sQuery(id+"F0.wireOp",EDGE,"E7.4.1.1"),sQuery(id+"F0.wireOp",EDGE,"E7.4.1.2"),sQuery(id+"F0.wireOp",EDGE,"E7.4.1.3"),sQuery(id+"F0.wireOp",EDGE,"E7.4.1.4"),sQuery(id+"F0.wireOp",EDGE,"E7.4.2.1"),sQuery(id+"F0.wireOp",EDGE,"E7.4.2.2"),sQuery(id+"F0.wireOp",EDGE,"E7.4.2.3"),sQuery(id+"F0.wireOp",EDGE,"E7.4.2.4"),sQuery(id+"F0.wireOp",EDGE,"E7.4.3.1"),sQuery(id+"F0.wireOp",EDGE,"E7.4.3.2"),sQuery(id+"F0.wireOp",EDGE,"E7.4.3.3"),sQuery(id+"F0.wireOp",EDGE,"E7.4.3.4"),sQuery(id+"F0.wireOp",EDGE,"E7.4.4.1"),sQuery(id+"F0.wireOp",EDGE,"E7.4.4.2"),sQuery(id+"F0.wireOp",EDGE,"E7.4.4.3"),sQuery(id+"F0.wireOp",EDGE,"E7.4.4.4"),sQuery(id+"F0.wireOp",EDGE,"E7.5.0.1"),sQuery(id+"F0.wireOp",EDGE,"E7.5.0.2"),sQuery(id+"F0.wireOp",EDGE,"E7.5.0.3"),sQuery(id+"F0.wireOp",EDGE,"E7.5.0.4"),sQuery(id+"F0.wireOp",EDGE,"E7.5.1.1"),sQuery(id+"F0.wireOp",EDGE,"E7.5.1.2"),sQuery(id+"F0.wireOp",EDGE,"E7.5.1.3"),sQuery(id+"F0.wireOp",EDGE,"E7.5.1.4"),sQuery(id+"F0.wireOp",EDGE,"E7.5.2.1"),sQuery(id+"F0.wireOp",EDGE,"E7.5.2.2"),sQuery(id+"F0.wireOp",EDGE,"E7.5.2.3"),sQuery(id+"F0.wireOp",EDGE,"E7.5.2.4"),sQuery(id+"F0.wireOp",EDGE,"E7.5.3.1"),sQuery(id+"F0.wireOp",EDGE,"E7.5.3.2"),sQuery(id+"F0.wireOp",EDGE,"E7.5.3.3"),sQuery(id+"F0.wireOp",EDGE,"E7.5.3.4"),sQuery(id+"F0.wireOp",EDGE,"E7.5.4.1"),sQuery(id+"F0.wireOp",EDGE,"E7.5.4.2"),sQuery(id+"F0.wireOp",EDGE,"E7.5.4.3"),sQuery(id+"F0.wireOp",EDGE,"E7.5.4.4"),sQuery(id+"F0.wireOp",EDGE,"E7.6.0.1"),sQuery(id+"F0.wireOp",EDGE,"E7.6.0.2"),sQuery(id+"F0.wireOp",EDGE,"E7.6.0.3"),sQuery(id+"F0.wireOp",EDGE,"E7.6.0.4"),sQuery(id+"F0.wireOp",EDGE,"E7.6.1.1"),sQuery(id+"F0.wireOp",EDGE,"E7.6.1.2"),sQuery(id+"F0.wireOp",EDGE,"E7.6.1.3"),sQuery(id+"F0.wireOp",EDGE,"E7.6.1.4"),sQuery(id+"F0.wireOp",EDGE,"E7.6.2.1"),sQuery(id+"F0.wireOp",EDGE,"E7.6.2.2"),sQuery(id+"F0.wireOp",EDGE,"E7.6.2.3"),sQuery(id+"F0.wireOp",EDGE,"E7.6.2.4"),sQuery(id+"F0.wireOp",EDGE,"E7.6.3.1"),sQuery(id+"F0.wireOp",EDGE,"E7.6.3.2"),sQuery(id+"F0.wireOp",EDGE,"E7.6.3.3"),sQuery(id+"F0.wireOp",EDGE,"E7.6.3.4"),sQuery(id+"F0.wireOp",EDGE,"E7.6.4.1"),sQuery(id+"F0.wireOp",EDGE,"E7.6.4.2"),sQuery(id+"F0.wireOp",EDGE,"E7.6.4.3"),sQuery(id+"F0.wireOp",EDGE,"E7.6.4.4"),sQuery(id+"F0.wireOp",EDGE,"E7.7.0.1"),sQuery(id+"F0.wireOp",EDGE,"E7.7.0.2"),sQuery(id+"F0.wireOp",EDGE,"E7.7.0.3"),sQuery(id+"F0.wireOp",EDGE,"E7.7.0.4"),sQuery(id+"F0.wireOp",EDGE,"E7.7.1.1"),sQuery(id+"F0.wireOp",EDGE,"E7.7.1.2"),sQuery(id+"F0.wireOp",EDGE,"E7.7.1.3"),sQuery(id+"F0.wireOp",EDGE,"E7.7.1.4"),sQuery(id+"F0.wireOp",EDGE,"E7.7.2.1"),sQuery(id+"F0.wireOp",EDGE,"E7.7.2.2"),sQuery(id+"F0.wireOp",EDGE,"E7.7.2.3"),sQuery(id+"F0.wireOp",EDGE,"E7.7.2.4"),sQuery(id+"F0.wireOp",EDGE,"E7.7.3.1"),sQuery(id+"F0.wireOp",EDGE,"E7.7.3.2"),sQuery(id+"F0.wireOp",EDGE,"E7.7.3.3"),sQuery(id+"F0.wireOp",EDGE,"E7.7.3.4"),sQuery(id+"F0.wireOp",EDGE,"E7.7.4.1"),sQuery(id+"F0.wireOp",EDGE,"E7.7.4.2"),sQuery(id+"F0.wireOp",EDGE,"E7.7.4.3"),sQuery(id+"F0.wireOp",EDGE,"E7.7.4.4")])],"isStart":true});
            var sketch = newSketch(context, id + "F2", { "sketchPlane" : qUnion([Q0])});
            skLineSegment(sketch, "E21", {"start": v(-152.34, 85) * mm, "end": v(153.2, 85) * mm, "construction": true});
            skPoint(sketch, "E21.startSnap0", {"position": v(-125, 85) * mm});
            skPoint(sketch, "E21.endSnap0", {"position": v(11, 85) * mm});
            skLineSegment(sketch, "E22.bottom", {"start": v(-112.5, 82.5) * mm, "end": v(-125.5, 82.5) * mm});
            skLineSegment(sketch, "E22.top", {"start": v(-112.5, 87.5) * mm, "end": v(-125.5, 87.5) * mm});
            skLineSegment(sketch, "E22.left", {"start": v(-112.5, 82.5) * mm, "end": v(-112.5, 87.5) * mm});
            skLineSegment(sketch, "E22.right", {"start": v(-125.5, 82.5) * mm, "end": v(-125.5, 87.5) * mm});
            skPoint(sketch, "E22.middle", {"position": v(-119, 85) * mm});
            skLineSegment(sketch, "E23.0.1.0", {"start": v(-152.34, 51) * mm, "end": v(153.2, 51) * mm, "construction": true});
            skLineSegment(sketch, "E23.0.1.1", {"start": v(-112.5, 48.5) * mm, "end": v(-125.5, 48.5) * mm});
            skLineSegment(sketch, "E23.0.1.2", {"start": v(-112.5, 53.5) * mm, "end": v(-125.5, 53.5) * mm});
            skPoint(sketch, "E23.0.1.3", {"position": v(-119, 51) * mm});
            skPoint(sketch, "E23.0.1.4", {"position": v(-125, 51) * mm});
            skLineSegment(sketch, "E23.0.1.5", {"start": v(-112.5, 48.5) * mm, "end": v(-112.5, 53.5) * mm});
            skLineSegment(sketch, "E23.0.1.6", {"start": v(-125.5, 48.5) * mm, "end": v(-125.5, 53.5) * mm});
            skLineSegment(sketch, "E23.0.2.0", {"start": v(-152.34, 17) * mm, "end": v(153.2, 17) * mm, "construction": true});
            skLineSegment(sketch, "E23.0.2.1", {"start": v(-112.5, 14.5) * mm, "end": v(-125.5, 14.5) * mm});
            skLineSegment(sketch, "E23.0.2.2", {"start": v(-112.5, 19.5) * mm, "end": v(-125.5, 19.5) * mm});
            skPoint(sketch, "E23.0.2.3", {"position": v(-119, 17) * mm});
            skPoint(sketch, "E23.0.2.4", {"position": v(-125, 17) * mm});
            skLineSegment(sketch, "E23.0.2.5", {"start": v(-112.5, 14.5) * mm, "end": v(-112.5, 19.5) * mm});
            skLineSegment(sketch, "E23.0.2.6", {"start": v(-125.5, 14.5) * mm, "end": v(-125.5, 19.5) * mm});
            skLineSegment(sketch, "E23.0.3.0", {"start": v(-152.34, -17) * mm, "end": v(153.2, -17) * mm, "construction": true});
            skLineSegment(sketch, "E23.0.3.1", {"start": v(-112.5, -19.5) * mm, "end": v(-125.5, -19.5) * mm});
            skLineSegment(sketch, "E23.0.3.2", {"start": v(-112.5, -14.5) * mm, "end": v(-125.5, -14.5) * mm});
            skPoint(sketch, "E23.0.3.3", {"position": v(-119, -17) * mm});
            skPoint(sketch, "E23.0.3.4", {"position": v(-125, -17) * mm});
            skLineSegment(sketch, "E23.0.3.5", {"start": v(-112.5, -19.5) * mm, "end": v(-112.5, -14.5) * mm});
            skLineSegment(sketch, "E23.0.3.6", {"start": v(-125.5, -19.5) * mm, "end": v(-125.5, -14.5) * mm});
            skLineSegment(sketch, "E23.0.4.0", {"start": v(-152.34, -51) * mm, "end": v(153.2, -51) * mm, "construction": true});
            skLineSegment(sketch, "E23.0.4.1", {"start": v(-112.5, -53.5) * mm, "end": v(-125.5, -53.5) * mm});
            skLineSegment(sketch, "E23.0.4.2", {"start": v(-112.5, -48.5) * mm, "end": v(-125.5, -48.5) * mm});
            skPoint(sketch, "E23.0.4.3", {"position": v(-119, -51) * mm});
            skPoint(sketch, "E23.0.4.4", {"position": v(-125, -51) * mm});
            skLineSegment(sketch, "E23.0.4.5", {"start": v(-112.5, -53.5) * mm, "end": v(-112.5, -48.5) * mm});
            skLineSegment(sketch, "E23.0.4.6", {"start": v(-125.5, -53.5) * mm, "end": v(-125.5, -48.5) * mm});
            skLineSegment(sketch, "E23.1.0.0", {"start": v(-118.34, 85) * mm, "end": v(187.2, 85) * mm, "construction": true});
            skLineSegment(sketch, "E23.1.0.1", {"start": v(-78.5, 82.5) * mm, "end": v(-91.5, 82.5) * mm});
            skLineSegment(sketch, "E23.1.0.2", {"start": v(-78.5, 87.5) * mm, "end": v(-91.5, 87.5) * mm});
            skPoint(sketch, "E23.1.0.3", {"position": v(-85, 85) * mm});
            skPoint(sketch, "E23.1.0.4", {"position": v(-91, 85) * mm});
            skLineSegment(sketch, "E23.1.0.5", {"start": v(-78.5, 82.5) * mm, "end": v(-78.5, 87.5) * mm});
            skLineSegment(sketch, "E23.1.0.6", {"start": v(-91.5, 82.5) * mm, "end": v(-91.5, 87.5) * mm});
            skLineSegment(sketch, "E23.1.1.0", {"start": v(-118.34, 51) * mm, "end": v(187.2, 51) * mm, "construction": true});
            skLineSegment(sketch, "E23.1.1.1", {"start": v(-78.5, 48.5) * mm, "end": v(-91.5, 48.5) * mm});
            skLineSegment(sketch, "E23.1.1.2", {"start": v(-78.5, 53.5) * mm, "end": v(-91.5, 53.5) * mm});
            skPoint(sketch, "E23.1.1.3", {"position": v(-85, 51) * mm});
            skPoint(sketch, "E23.1.1.4", {"position": v(-91, 51) * mm});
            skLineSegment(sketch, "E23.1.1.5", {"start": v(-78.5, 48.5) * mm, "end": v(-78.5, 53.5) * mm});
            skLineSegment(sketch, "E23.1.1.6", {"start": v(-91.5, 48.5) * mm, "end": v(-91.5, 53.5) * mm});
            skLineSegment(sketch, "E23.1.2.0", {"start": v(-118.34, 17) * mm, "end": v(187.2, 17) * mm, "construction": true});
            skLineSegment(sketch, "E23.1.2.1", {"start": v(-78.5, 14.5) * mm, "end": v(-91.5, 14.5) * mm});
            skLineSegment(sketch, "E23.1.2.2", {"start": v(-78.5, 19.5) * mm, "end": v(-91.5, 19.5) * mm});
            skPoint(sketch, "E23.1.2.3", {"position": v(-85, 17) * mm});
            skPoint(sketch, "E23.1.2.4", {"position": v(-91, 17) * mm});
            skLineSegment(sketch, "E23.1.2.5", {"start": v(-78.5, 14.5) * mm, "end": v(-78.5, 19.5) * mm});
            skLineSegment(sketch, "E23.1.2.6", {"start": v(-91.5, 14.5) * mm, "end": v(-91.5, 19.5) * mm});
            skLineSegment(sketch, "E23.1.3.0", {"start": v(-118.34, -17) * mm, "end": v(187.2, -17) * mm, "construction": true});
            skLineSegment(sketch, "E23.1.3.1", {"start": v(-78.5, -19.5) * mm, "end": v(-91.5, -19.5) * mm});
            skLineSegment(sketch, "E23.1.3.2", {"start": v(-78.5, -14.5) * mm, "end": v(-91.5, -14.5) * mm});
            skPoint(sketch, "E23.1.3.3", {"position": v(-85, -17) * mm});
            skPoint(sketch, "E23.1.3.4", {"position": v(-91, -17) * mm});
            skLineSegment(sketch, "E23.1.3.5", {"start": v(-78.5, -19.5) * mm, "end": v(-78.5, -14.5) * mm});
            skLineSegment(sketch, "E23.1.3.6", {"start": v(-91.5, -19.5) * mm, "end": v(-91.5, -14.5) * mm});
            skLineSegment(sketch, "E23.1.4.0", {"start": v(-118.34, -51) * mm, "end": v(187.2, -51) * mm, "construction": true});
            skLineSegment(sketch, "E23.1.4.1", {"start": v(-78.5, -53.5) * mm, "end": v(-91.5, -53.5) * mm});
            skLineSegment(sketch, "E23.1.4.2", {"start": v(-78.5, -48.5) * mm, "end": v(-91.5, -48.5) * mm});
            skPoint(sketch, "E23.1.4.3", {"position": v(-85, -51) * mm});
            skPoint(sketch, "E23.1.4.4", {"position": v(-91, -51) * mm});
            skLineSegment(sketch, "E23.1.4.5", {"start": v(-78.5, -53.5) * mm, "end": v(-78.5, -48.5) * mm});
            skLineSegment(sketch, "E23.1.4.6", {"start": v(-91.5, -53.5) * mm, "end": v(-91.5, -48.5) * mm});
            skLineSegment(sketch, "E23.2.0.0", {"start": v(-84.34, 85) * mm, "end": v(221.2, 85) * mm, "construction": true});
            skLineSegment(sketch, "E23.2.0.1", {"start": v(-44.5, 82.5) * mm, "end": v(-57.5, 82.5) * mm});
            skLineSegment(sketch, "E23.2.0.2", {"start": v(-44.5, 87.5) * mm, "end": v(-57.5, 87.5) * mm});
            skPoint(sketch, "E23.2.0.3", {"position": v(-51, 85) * mm});
            skPoint(sketch, "E23.2.0.4", {"position": v(-57, 85) * mm});
            skLineSegment(sketch, "E23.2.0.5", {"start": v(-44.5, 82.5) * mm, "end": v(-44.5, 87.5) * mm});
            skLineSegment(sketch, "E23.2.0.6", {"start": v(-57.5, 82.5) * mm, "end": v(-57.5, 87.5) * mm});
            skLineSegment(sketch, "E23.2.1.0", {"start": v(-84.34, 51) * mm, "end": v(221.2, 51) * mm, "construction": true});
            skLineSegment(sketch, "E23.2.1.1", {"start": v(-44.5, 48.5) * mm, "end": v(-57.5, 48.5) * mm});
            skLineSegment(sketch, "E23.2.1.2", {"start": v(-44.5, 53.5) * mm, "end": v(-57.5, 53.5) * mm});
            skPoint(sketch, "E23.2.1.3", {"position": v(-51, 51) * mm});
            skPoint(sketch, "E23.2.1.4", {"position": v(-57, 51) * mm});
            skLineSegment(sketch, "E23.2.1.5", {"start": v(-44.5, 48.5) * mm, "end": v(-44.5, 53.5) * mm});
            skLineSegment(sketch, "E23.2.1.6", {"start": v(-57.5, 48.5) * mm, "end": v(-57.5, 53.5) * mm});
            skLineSegment(sketch, "E23.2.2.0", {"start": v(-84.34, 17) * mm, "end": v(221.2, 17) * mm, "construction": true});
            skLineSegment(sketch, "E23.2.2.1", {"start": v(-44.5, 14.5) * mm, "end": v(-57.5, 14.5) * mm});
            skLineSegment(sketch, "E23.2.2.2", {"start": v(-44.5, 19.5) * mm, "end": v(-57.5, 19.5) * mm});
            skPoint(sketch, "E23.2.2.3", {"position": v(-51, 17) * mm});
            skPoint(sketch, "E23.2.2.4", {"position": v(-57, 17) * mm});
            skLineSegment(sketch, "E23.2.2.5", {"start": v(-44.5, 14.5) * mm, "end": v(-44.5, 19.5) * mm});
            skLineSegment(sketch, "E23.2.2.6", {"start": v(-57.5, 14.5) * mm, "end": v(-57.5, 19.5) * mm});
            skLineSegment(sketch, "E23.2.3.0", {"start": v(-84.34, -17) * mm, "end": v(221.2, -17) * mm, "construction": true});
            skLineSegment(sketch, "E23.2.3.1", {"start": v(-44.5, -19.5) * mm, "end": v(-57.5, -19.5) * mm});
            skLineSegment(sketch, "E23.2.3.2", {"start": v(-44.5, -14.5) * mm, "end": v(-57.5, -14.5) * mm});
            skPoint(sketch, "E23.2.3.3", {"position": v(-51, -17) * mm});
            skPoint(sketch, "E23.2.3.4", {"position": v(-57, -17) * mm});
            skLineSegment(sketch, "E23.2.3.5", {"start": v(-44.5, -19.5) * mm, "end": v(-44.5, -14.5) * mm});
            skLineSegment(sketch, "E23.2.3.6", {"start": v(-57.5, -19.5) * mm, "end": v(-57.5, -14.5) * mm});
            skLineSegment(sketch, "E23.2.4.0", {"start": v(-84.34, -51) * mm, "end": v(221.2, -51) * mm, "construction": true});
            skLineSegment(sketch, "E23.2.4.1", {"start": v(-44.5, -53.5) * mm, "end": v(-57.5, -53.5) * mm});
            skLineSegment(sketch, "E23.2.4.2", {"start": v(-44.5, -48.5) * mm, "end": v(-57.5, -48.5) * mm});
            skPoint(sketch, "E23.2.4.3", {"position": v(-51, -51) * mm});
            skPoint(sketch, "E23.2.4.4", {"position": v(-57, -51) * mm});
            skLineSegment(sketch, "E23.2.4.5", {"start": v(-44.5, -53.5) * mm, "end": v(-44.5, -48.5) * mm});
            skLineSegment(sketch, "E23.2.4.6", {"start": v(-57.5, -53.5) * mm, "end": v(-57.5, -48.5) * mm});
            skLineSegment(sketch, "E23.3.0.0", {"start": v(-50.34, 85) * mm, "end": v(255.2, 85) * mm, "construction": true});
            skLineSegment(sketch, "E23.3.0.1", {"start": v(-10.5, 82.5) * mm, "end": v(-23.5, 82.5) * mm});
            skLineSegment(sketch, "E23.3.0.2", {"start": v(-10.5, 87.5) * mm, "end": v(-23.5, 87.5) * mm});
            skPoint(sketch, "E23.3.0.3", {"position": v(-17, 85) * mm});
            skPoint(sketch, "E23.3.0.4", {"position": v(-23, 85) * mm});
            skLineSegment(sketch, "E23.3.0.5", {"start": v(-10.5, 82.5) * mm, "end": v(-10.5, 87.5) * mm});
            skLineSegment(sketch, "E23.3.0.6", {"start": v(-23.5, 82.5) * mm, "end": v(-23.5, 87.5) * mm});
            skLineSegment(sketch, "E23.3.1.0", {"start": v(-50.34, 51) * mm, "end": v(255.2, 51) * mm, "construction": true});
            skLineSegment(sketch, "E23.3.1.1", {"start": v(-10.5, 48.5) * mm, "end": v(-23.5, 48.5) * mm});
            skLineSegment(sketch, "E23.3.1.2", {"start": v(-10.5, 53.5) * mm, "end": v(-23.5, 53.5) * mm});
            skPoint(sketch, "E23.3.1.3", {"position": v(-17, 51) * mm});
            skPoint(sketch, "E23.3.1.4", {"position": v(-23, 51) * mm});
            skLineSegment(sketch, "E23.3.1.5", {"start": v(-10.5, 48.5) * mm, "end": v(-10.5, 53.5) * mm});
            skLineSegment(sketch, "E23.3.1.6", {"start": v(-23.5, 48.5) * mm, "end": v(-23.5, 53.5) * mm});
            skLineSegment(sketch, "E23.3.2.0", {"start": v(-50.34, 17) * mm, "end": v(255.2, 17) * mm, "construction": true});
            skLineSegment(sketch, "E23.3.2.1", {"start": v(-10.5, 14.5) * mm, "end": v(-23.5, 14.5) * mm});
            skLineSegment(sketch, "E23.3.2.2", {"start": v(-10.5, 19.5) * mm, "end": v(-23.5, 19.5) * mm});
            skPoint(sketch, "E23.3.2.3", {"position": v(-17, 17) * mm});
            skPoint(sketch, "E23.3.2.4", {"position": v(-23, 17) * mm});
            skLineSegment(sketch, "E23.3.2.5", {"start": v(-10.5, 14.5) * mm, "end": v(-10.5, 19.5) * mm});
            skLineSegment(sketch, "E23.3.2.6", {"start": v(-23.5, 14.5) * mm, "end": v(-23.5, 19.5) * mm});
            skLineSegment(sketch, "E23.3.3.0", {"start": v(-50.34, -17) * mm, "end": v(255.2, -17) * mm, "construction": true});
            skLineSegment(sketch, "E23.3.3.1", {"start": v(-10.5, -19.5) * mm, "end": v(-23.5, -19.5) * mm});
            skLineSegment(sketch, "E23.3.3.2", {"start": v(-10.5, -14.5) * mm, "end": v(-23.5, -14.5) * mm});
            skPoint(sketch, "E23.3.3.3", {"position": v(-17, -17) * mm});
            skPoint(sketch, "E23.3.3.4", {"position": v(-23, -17) * mm});
            skLineSegment(sketch, "E23.3.3.5", {"start": v(-10.5, -19.5) * mm, "end": v(-10.5, -14.5) * mm});
            skLineSegment(sketch, "E23.3.3.6", {"start": v(-23.5, -19.5) * mm, "end": v(-23.5, -14.5) * mm});
            skLineSegment(sketch, "E23.3.4.0", {"start": v(-50.34, -51) * mm, "end": v(255.2, -51) * mm, "construction": true});
            skLineSegment(sketch, "E23.3.4.1", {"start": v(-10.5, -53.5) * mm, "end": v(-23.5, -53.5) * mm});
            skLineSegment(sketch, "E23.3.4.2", {"start": v(-10.5, -48.5) * mm, "end": v(-23.5, -48.5) * mm});
            skPoint(sketch, "E23.3.4.3", {"position": v(-17, -51) * mm});
            skPoint(sketch, "E23.3.4.4", {"position": v(-23, -51) * mm});
            skLineSegment(sketch, "E23.3.4.5", {"start": v(-10.5, -53.5) * mm, "end": v(-10.5, -48.5) * mm});
            skLineSegment(sketch, "E23.3.4.6", {"start": v(-23.5, -53.5) * mm, "end": v(-23.5, -48.5) * mm});
            skLineSegment(sketch, "E23.4.0.0", {"start": v(-16.34, 85) * mm, "end": v(289.2, 85) * mm, "construction": true});
            skLineSegment(sketch, "E23.4.0.1", {"start": v(23.5, 82.5) * mm, "end": v(10.5, 82.5) * mm});
            skLineSegment(sketch, "E23.4.0.2", {"start": v(23.5, 87.5) * mm, "end": v(10.5, 87.5) * mm});
            skPoint(sketch, "E23.4.0.3", {"position": v(17, 85) * mm});
            skLineSegment(sketch, "E23.4.0.5", {"start": v(23.5, 82.5) * mm, "end": v(23.5, 87.5) * mm});
            skLineSegment(sketch, "E23.4.0.6", {"start": v(10.5, 82.5) * mm, "end": v(10.5, 87.5) * mm});
            skLineSegment(sketch, "E23.4.1.0", {"start": v(-16.34, 51) * mm, "end": v(289.2, 51) * mm, "construction": true});
            skLineSegment(sketch, "E23.4.1.1", {"start": v(23.5, 48.5) * mm, "end": v(10.5, 48.5) * mm});
            skLineSegment(sketch, "E23.4.1.2", {"start": v(23.5, 53.5) * mm, "end": v(10.5, 53.5) * mm});
            skPoint(sketch, "E23.4.1.3", {"position": v(17, 51) * mm});
            skPoint(sketch, "E23.4.1.4", {"position": v(11, 51) * mm});
            skLineSegment(sketch, "E23.4.1.5", {"start": v(23.5, 48.5) * mm, "end": v(23.5, 53.5) * mm});
            skLineSegment(sketch, "E23.4.1.6", {"start": v(10.5, 48.5) * mm, "end": v(10.5, 53.5) * mm});
            skLineSegment(sketch, "E23.4.2.0", {"start": v(-16.34, 17) * mm, "end": v(289.2, 17) * mm, "construction": true});
            skLineSegment(sketch, "E23.4.2.1", {"start": v(23.5, 14.5) * mm, "end": v(10.5, 14.5) * mm});
            skLineSegment(sketch, "E23.4.2.2", {"start": v(23.5, 19.5) * mm, "end": v(10.5, 19.5) * mm});
            skPoint(sketch, "E23.4.2.3", {"position": v(17, 17) * mm});
            skPoint(sketch, "E23.4.2.4", {"position": v(11, 17) * mm});
            skLineSegment(sketch, "E23.4.2.5", {"start": v(23.5, 14.5) * mm, "end": v(23.5, 19.5) * mm});
            skLineSegment(sketch, "E23.4.2.6", {"start": v(10.5, 14.5) * mm, "end": v(10.5, 19.5) * mm});
            skLineSegment(sketch, "E23.4.3.0", {"start": v(-16.34, -17) * mm, "end": v(289.2, -17) * mm, "construction": true});
            skLineSegment(sketch, "E23.4.3.1", {"start": v(23.5, -19.5) * mm, "end": v(10.5, -19.5) * mm});
            skLineSegment(sketch, "E23.4.3.2", {"start": v(23.5, -14.5) * mm, "end": v(10.5, -14.5) * mm});
            skPoint(sketch, "E23.4.3.3", {"position": v(17, -17) * mm});
            skPoint(sketch, "E23.4.3.4", {"position": v(11, -17) * mm});
            skLineSegment(sketch, "E23.4.3.5", {"start": v(23.5, -19.5) * mm, "end": v(23.5, -14.5) * mm});
            skLineSegment(sketch, "E23.4.3.6", {"start": v(10.5, -19.5) * mm, "end": v(10.5, -14.5) * mm});
            skLineSegment(sketch, "E23.4.4.0", {"start": v(-16.34, -51) * mm, "end": v(289.2, -51) * mm, "construction": true});
            skLineSegment(sketch, "E23.4.4.1", {"start": v(23.5, -53.5) * mm, "end": v(10.5, -53.5) * mm});
            skLineSegment(sketch, "E23.4.4.2", {"start": v(23.5, -48.5) * mm, "end": v(10.5, -48.5) * mm});
            skPoint(sketch, "E23.4.4.3", {"position": v(17, -51) * mm});
            skPoint(sketch, "E23.4.4.4", {"position": v(11, -51) * mm});
            skLineSegment(sketch, "E23.4.4.5", {"start": v(23.5, -53.5) * mm, "end": v(23.5, -48.5) * mm});
            skLineSegment(sketch, "E23.4.4.6", {"start": v(10.5, -53.5) * mm, "end": v(10.5, -48.5) * mm});
            skLineSegment(sketch, "E23.5.0.0", {"start": v(17.66, 85) * mm, "end": v(323.2, 85) * mm, "construction": true});
            skLineSegment(sketch, "E23.5.0.1", {"start": v(57.5, 82.5) * mm, "end": v(44.5, 82.5) * mm});
            skLineSegment(sketch, "E23.5.0.2", {"start": v(57.5, 87.5) * mm, "end": v(44.5, 87.5) * mm});
            skPoint(sketch, "E23.5.0.3", {"position": v(51, 85) * mm});
            skPoint(sketch, "E23.5.0.4", {"position": v(45, 85) * mm});
            skLineSegment(sketch, "E23.5.0.5", {"start": v(57.5, 82.5) * mm, "end": v(57.5, 87.5) * mm});
            skLineSegment(sketch, "E23.5.0.6", {"start": v(44.5, 82.5) * mm, "end": v(44.5, 87.5) * mm});
            skLineSegment(sketch, "E23.5.1.0", {"start": v(17.66, 51) * mm, "end": v(323.2, 51) * mm, "construction": true});
            skLineSegment(sketch, "E23.5.1.1", {"start": v(57.5, 48.5) * mm, "end": v(44.5, 48.5) * mm});
            skLineSegment(sketch, "E23.5.1.2", {"start": v(57.5, 53.5) * mm, "end": v(44.5, 53.5) * mm});
            skPoint(sketch, "E23.5.1.3", {"position": v(51, 51) * mm});
            skPoint(sketch, "E23.5.1.4", {"position": v(45, 51) * mm});
            skLineSegment(sketch, "E23.5.1.5", {"start": v(57.5, 48.5) * mm, "end": v(57.5, 53.5) * mm});
            skLineSegment(sketch, "E23.5.1.6", {"start": v(44.5, 48.5) * mm, "end": v(44.5, 53.5) * mm});
            skLineSegment(sketch, "E23.5.2.0", {"start": v(17.66, 17) * mm, "end": v(323.2, 17) * mm, "construction": true});
            skLineSegment(sketch, "E23.5.2.1", {"start": v(57.5, 14.5) * mm, "end": v(44.5, 14.5) * mm});
            skLineSegment(sketch, "E23.5.2.2", {"start": v(57.5, 19.5) * mm, "end": v(44.5, 19.5) * mm});
            skPoint(sketch, "E23.5.2.3", {"position": v(51, 17) * mm});
            skPoint(sketch, "E23.5.2.4", {"position": v(45, 17) * mm});
            skLineSegment(sketch, "E23.5.2.5", {"start": v(57.5, 14.5) * mm, "end": v(57.5, 19.5) * mm});
            skLineSegment(sketch, "E23.5.2.6", {"start": v(44.5, 14.5) * mm, "end": v(44.5, 19.5) * mm});
            skLineSegment(sketch, "E23.5.3.0", {"start": v(17.66, -17) * mm, "end": v(323.2, -17) * mm, "construction": true});
            skLineSegment(sketch, "E23.5.3.1", {"start": v(57.5, -19.5) * mm, "end": v(44.5, -19.5) * mm});
            skLineSegment(sketch, "E23.5.3.2", {"start": v(57.5, -14.5) * mm, "end": v(44.5, -14.5) * mm});
            skPoint(sketch, "E23.5.3.3", {"position": v(51, -17) * mm});
            skPoint(sketch, "E23.5.3.4", {"position": v(45, -17) * mm});
            skLineSegment(sketch, "E23.5.3.5", {"start": v(57.5, -19.5) * mm, "end": v(57.5, -14.5) * mm});
            skLineSegment(sketch, "E23.5.3.6", {"start": v(44.5, -19.5) * mm, "end": v(44.5, -14.5) * mm});
            skLineSegment(sketch, "E23.5.4.0", {"start": v(17.66, -51) * mm, "end": v(323.2, -51) * mm, "construction": true});
            skLineSegment(sketch, "E23.5.4.1", {"start": v(57.5, -53.5) * mm, "end": v(44.5, -53.5) * mm});
            skLineSegment(sketch, "E23.5.4.2", {"start": v(57.5, -48.5) * mm, "end": v(44.5, -48.5) * mm});
            skPoint(sketch, "E23.5.4.3", {"position": v(51, -51) * mm});
            skPoint(sketch, "E23.5.4.4", {"position": v(45, -51) * mm});
            skLineSegment(sketch, "E23.5.4.5", {"start": v(57.5, -53.5) * mm, "end": v(57.5, -48.5) * mm});
            skLineSegment(sketch, "E23.5.4.6", {"start": v(44.5, -53.5) * mm, "end": v(44.5, -48.5) * mm});
            skLineSegment(sketch, "E23.6.0.0", {"start": v(51.66, 85) * mm, "end": v(357.2, 85) * mm, "construction": true});
            skLineSegment(sketch, "E23.6.0.1", {"start": v(91.5, 82.5) * mm, "end": v(78.5, 82.5) * mm});
            skLineSegment(sketch, "E23.6.0.2", {"start": v(91.5, 87.5) * mm, "end": v(78.5, 87.5) * mm});
            skPoint(sketch, "E23.6.0.3", {"position": v(85, 85) * mm});
            skPoint(sketch, "E23.6.0.4", {"position": v(79, 85) * mm});
            skLineSegment(sketch, "E23.6.0.5", {"start": v(91.5, 82.5) * mm, "end": v(91.5, 87.5) * mm});
            skLineSegment(sketch, "E23.6.0.6", {"start": v(78.5, 82.5) * mm, "end": v(78.5, 87.5) * mm});
            skLineSegment(sketch, "E23.6.1.0", {"start": v(51.66, 51) * mm, "end": v(357.2, 51) * mm, "construction": true});
            skLineSegment(sketch, "E23.6.1.1", {"start": v(91.5, 48.5) * mm, "end": v(78.5, 48.5) * mm});
            skLineSegment(sketch, "E23.6.1.2", {"start": v(91.5, 53.5) * mm, "end": v(78.5, 53.5) * mm});
            skPoint(sketch, "E23.6.1.3", {"position": v(85, 51) * mm});
            skPoint(sketch, "E23.6.1.4", {"position": v(79, 51) * mm});
            skLineSegment(sketch, "E23.6.1.5", {"start": v(91.5, 48.5) * mm, "end": v(91.5, 53.5) * mm});
            skLineSegment(sketch, "E23.6.1.6", {"start": v(78.5, 48.5) * mm, "end": v(78.5, 53.5) * mm});
            skLineSegment(sketch, "E23.6.2.0", {"start": v(51.66, 17) * mm, "end": v(357.2, 17) * mm, "construction": true});
            skLineSegment(sketch, "E23.6.2.1", {"start": v(91.5, 14.5) * mm, "end": v(78.5, 14.5) * mm});
            skLineSegment(sketch, "E23.6.2.2", {"start": v(91.5, 19.5) * mm, "end": v(78.5, 19.5) * mm});
            skPoint(sketch, "E23.6.2.3", {"position": v(85, 17) * mm});
            skPoint(sketch, "E23.6.2.4", {"position": v(79, 17) * mm});
            skLineSegment(sketch, "E23.6.2.5", {"start": v(91.5, 14.5) * mm, "end": v(91.5, 19.5) * mm});
            skLineSegment(sketch, "E23.6.2.6", {"start": v(78.5, 14.5) * mm, "end": v(78.5, 19.5) * mm});
            skLineSegment(sketch, "E23.6.3.0", {"start": v(51.66, -17) * mm, "end": v(357.2, -17) * mm, "construction": true});
            skLineSegment(sketch, "E23.6.3.1", {"start": v(91.5, -19.5) * mm, "end": v(78.5, -19.5) * mm});
            skLineSegment(sketch, "E23.6.3.2", {"start": v(91.5, -14.5) * mm, "end": v(78.5, -14.5) * mm});
            skPoint(sketch, "E23.6.3.3", {"position": v(85, -17) * mm});
            skPoint(sketch, "E23.6.3.4", {"position": v(79, -17) * mm});
            skLineSegment(sketch, "E23.6.3.5", {"start": v(91.5, -19.5) * mm, "end": v(91.5, -14.5) * mm});
            skLineSegment(sketch, "E23.6.3.6", {"start": v(78.5, -19.5) * mm, "end": v(78.5, -14.5) * mm});
            skLineSegment(sketch, "E23.6.4.0", {"start": v(51.66, -51) * mm, "end": v(357.2, -51) * mm, "construction": true});
            skLineSegment(sketch, "E23.6.4.1", {"start": v(91.5, -53.5) * mm, "end": v(78.5, -53.5) * mm});
            skLineSegment(sketch, "E23.6.4.2", {"start": v(91.5, -48.5) * mm, "end": v(78.5, -48.5) * mm});
            skPoint(sketch, "E23.6.4.3", {"position": v(85, -51) * mm});
            skPoint(sketch, "E23.6.4.4", {"position": v(79, -51) * mm});
            skLineSegment(sketch, "E23.6.4.5", {"start": v(91.5, -53.5) * mm, "end": v(91.5, -48.5) * mm});
            skLineSegment(sketch, "E23.6.4.6", {"start": v(78.5, -53.5) * mm, "end": v(78.5, -48.5) * mm});
            skLineSegment(sketch, "E23.7.0.0", {"start": v(85.66, 85) * mm, "end": v(391.2, 85) * mm, "construction": true});
            skLineSegment(sketch, "E23.7.0.1", {"start": v(125.5, 82.5) * mm, "end": v(112.5, 82.5) * mm});
            skLineSegment(sketch, "E23.7.0.2", {"start": v(125.5, 87.5) * mm, "end": v(112.5, 87.5) * mm});
            skPoint(sketch, "E23.7.0.3", {"position": v(119, 85) * mm});
            skPoint(sketch, "E23.7.0.4", {"position": v(113, 85) * mm});
            skLineSegment(sketch, "E23.7.0.5", {"start": v(125.5, 82.5) * mm, "end": v(125.5, 87.5) * mm});
            skLineSegment(sketch, "E23.7.0.6", {"start": v(112.5, 82.5) * mm, "end": v(112.5, 87.5) * mm});
            skLineSegment(sketch, "E23.7.1.0", {"start": v(85.66, 51) * mm, "end": v(391.2, 51) * mm, "construction": true});
            skLineSegment(sketch, "E23.7.1.1", {"start": v(125.5, 48.5) * mm, "end": v(112.5, 48.5) * mm});
            skLineSegment(sketch, "E23.7.1.2", {"start": v(125.5, 53.5) * mm, "end": v(112.5, 53.5) * mm});
            skPoint(sketch, "E23.7.1.3", {"position": v(119, 51) * mm});
            skPoint(sketch, "E23.7.1.4", {"position": v(113, 51) * mm});
            skLineSegment(sketch, "E23.7.1.5", {"start": v(125.5, 48.5) * mm, "end": v(125.5, 53.5) * mm});
            skLineSegment(sketch, "E23.7.1.6", {"start": v(112.5, 48.5) * mm, "end": v(112.5, 53.5) * mm});
            skLineSegment(sketch, "E23.7.2.0", {"start": v(85.66, 17) * mm, "end": v(391.2, 17) * mm, "construction": true});
            skLineSegment(sketch, "E23.7.2.1", {"start": v(125.5, 14.5) * mm, "end": v(112.5, 14.5) * mm});
            skLineSegment(sketch, "E23.7.2.2", {"start": v(125.5, 19.5) * mm, "end": v(112.5, 19.5) * mm});
            skPoint(sketch, "E23.7.2.3", {"position": v(119, 17) * mm});
            skPoint(sketch, "E23.7.2.4", {"position": v(113, 17) * mm});
            skLineSegment(sketch, "E23.7.2.5", {"start": v(125.5, 14.5) * mm, "end": v(125.5, 19.5) * mm});
            skLineSegment(sketch, "E23.7.2.6", {"start": v(112.5, 14.5) * mm, "end": v(112.5, 19.5) * mm});
            skLineSegment(sketch, "E23.7.3.0", {"start": v(85.66, -17) * mm, "end": v(391.2, -17) * mm, "construction": true});
            skLineSegment(sketch, "E23.7.3.1", {"start": v(125.5, -19.5) * mm, "end": v(112.5, -19.5) * mm});
            skLineSegment(sketch, "E23.7.3.2", {"start": v(125.5, -14.5) * mm, "end": v(112.5, -14.5) * mm});
            skPoint(sketch, "E23.7.3.3", {"position": v(119, -17) * mm});
            skPoint(sketch, "E23.7.3.4", {"position": v(113, -17) * mm});
            skLineSegment(sketch, "E23.7.3.5", {"start": v(125.5, -19.5) * mm, "end": v(125.5, -14.5) * mm});
            skLineSegment(sketch, "E23.7.3.6", {"start": v(112.5, -19.5) * mm, "end": v(112.5, -14.5) * mm});
            skLineSegment(sketch, "E23.7.4.0", {"start": v(85.66, -51) * mm, "end": v(391.2, -51) * mm, "construction": true});
            skLineSegment(sketch, "E23.7.4.1", {"start": v(125.5, -53.5) * mm, "end": v(112.5, -53.5) * mm});
            skLineSegment(sketch, "E23.7.4.2", {"start": v(125.5, -48.5) * mm, "end": v(112.5, -48.5) * mm});
            skPoint(sketch, "E23.7.4.3", {"position": v(119, -51) * mm});
            skPoint(sketch, "E23.7.4.4", {"position": v(113, -51) * mm});
            skLineSegment(sketch, "E23.7.4.5", {"start": v(125.5, -53.5) * mm, "end": v(125.5, -48.5) * mm});
            skLineSegment(sketch, "E23.7.4.6", {"start": v(112.5, -53.5) * mm, "end": v(112.5, -48.5) * mm});
            skLineSegment(sketch, "E23.direction1", {"start": v(-152.34, 85) * mm, "end": v(-118.34, 85) * mm, "construction": true});
            skLineSegment(sketch, "E23.direction2", {"start": v(-152.34, 85) * mm, "end": v(-152.34, 51) * mm, "construction": true});
            skCircle(sketch, "E24", {"center": v(-119, 85) * mm, "radius": 1.5 * mm});
            skCircle(sketch, "E25.0.1.1", {"center": v(-119, 51) * mm, "radius": 1.5 * mm});
            skCircle(sketch, "E25.0.2.1", {"center": v(-119, 17) * mm, "radius": 1.5 * mm});
            skCircle(sketch, "E25.0.3.1", {"center": v(-119, -17) * mm, "radius": 1.5 * mm});
            skCircle(sketch, "E25.0.4.1", {"center": v(-119, -51) * mm, "radius": 1.5 * mm});
            skCircle(sketch, "E25.1.0.1", {"center": v(-85, 85) * mm, "radius": 1.5 * mm});
            skCircle(sketch, "E25.1.1.1", {"center": v(-85, 51) * mm, "radius": 1.5 * mm});
            skCircle(sketch, "E25.1.2.1", {"center": v(-85, 17) * mm, "radius": 1.5 * mm});
            skCircle(sketch, "E25.1.3.1", {"center": v(-85, -17) * mm, "radius": 1.5 * mm});
            skCircle(sketch, "E25.1.4.1", {"center": v(-85, -51) * mm, "radius": 1.5 * mm});
            skCircle(sketch, "E25.2.0.1", {"center": v(-51, 85) * mm, "radius": 1.5 * mm});
            skCircle(sketch, "E25.2.1.1", {"center": v(-51, 51) * mm, "radius": 1.5 * mm});
            skCircle(sketch, "E25.2.2.1", {"center": v(-51, 17) * mm, "radius": 1.5 * mm});
            skCircle(sketch, "E25.2.3.1", {"center": v(-51, -17) * mm, "radius": 1.5 * mm});
            skCircle(sketch, "E25.2.4.1", {"center": v(-51, -51) * mm, "radius": 1.5 * mm});
            skCircle(sketch, "E25.3.0.1", {"center": v(-17, 85) * mm, "radius": 1.5 * mm});
            skCircle(sketch, "E25.3.1.1", {"center": v(-17, 51) * mm, "radius": 1.5 * mm});
            skCircle(sketch, "E25.3.2.1", {"center": v(-17, 17) * mm, "radius": 1.5 * mm});
            skCircle(sketch, "E25.3.3.1", {"center": v(-17, -17) * mm, "radius": 1.5 * mm});
            skCircle(sketch, "E25.3.4.1", {"center": v(-17, -51) * mm, "radius": 1.5 * mm});
            skCircle(sketch, "E25.4.0.1", {"center": v(17, 85) * mm, "radius": 1.5 * mm});
            skCircle(sketch, "E25.4.1.1", {"center": v(17, 51) * mm, "radius": 1.5 * mm});
            skCircle(sketch, "E25.4.2.1", {"center": v(17, 17) * mm, "radius": 1.5 * mm});
            skCircle(sketch, "E25.4.3.1", {"center": v(17, -17) * mm, "radius": 1.5 * mm});
            skCircle(sketch, "E25.4.4.1", {"center": v(17, -51) * mm, "radius": 1.5 * mm});
            skCircle(sketch, "E25.5.0.1", {"center": v(51, 85) * mm, "radius": 1.5 * mm});
            skCircle(sketch, "E25.5.1.1", {"center": v(51, 51) * mm, "radius": 1.5 * mm});
            skCircle(sketch, "E25.5.2.1", {"center": v(51, 17) * mm, "radius": 1.5 * mm});
            skCircle(sketch, "E25.5.3.1", {"center": v(51, -17) * mm, "radius": 1.5 * mm});
            skCircle(sketch, "E25.5.4.1", {"center": v(51, -51) * mm, "radius": 1.5 * mm});
            skCircle(sketch, "E25.6.0.1", {"center": v(85, 85) * mm, "radius": 1.5 * mm});
            skCircle(sketch, "E25.6.1.1", {"center": v(85, 51) * mm, "radius": 1.5 * mm});
            skCircle(sketch, "E25.6.2.1", {"center": v(85, 17) * mm, "radius": 1.5 * mm});
            skCircle(sketch, "E25.6.3.1", {"center": v(85, -17) * mm, "radius": 1.5 * mm});
            skCircle(sketch, "E25.6.4.1", {"center": v(85, -51) * mm, "radius": 1.5 * mm});
            skCircle(sketch, "E25.7.0.1", {"center": v(119, 85) * mm, "radius": 1.5 * mm});
            skCircle(sketch, "E25.7.1.1", {"center": v(119, 51) * mm, "radius": 1.5 * mm});
            skCircle(sketch, "E25.7.2.1", {"center": v(119, 17) * mm, "radius": 1.5 * mm});
            skCircle(sketch, "E25.7.3.1", {"center": v(119, -17) * mm, "radius": 1.5 * mm});
            skCircle(sketch, "E25.7.4.1", {"center": v(119, -51) * mm, "radius": 1.5 * mm});
            skLineSegment(sketch, "E26.0.0.5", {"start": v(-152.34, -85) * mm, "end": v(153.2, -85) * mm, "construction": true});
            skLineSegment(sketch, "E26.3.0.5", {"start": v(-112.5, -87.5) * mm, "end": v(-125.5, -87.5) * mm});
            skLineSegment(sketch, "E26.6.0.5", {"start": v(-112.5, -82.5) * mm, "end": v(-125.5, -82.5) * mm});
            skPoint(sketch, "E26.9.0.5", {"position": v(-119, -85) * mm});
            skPoint(sketch, "E26.10.0.5", {"position": v(-125, -85) * mm});
            skLineSegment(sketch, "E26.11.0.5", {"start": v(-112.5, -87.5) * mm, "end": v(-112.5, -82.5) * mm});
            skLineSegment(sketch, "E26.14.0.5", {"start": v(-125.5, -87.5) * mm, "end": v(-125.5, -82.5) * mm});
            skLineSegment(sketch, "E26.0.1.5", {"start": v(-118.34, -85) * mm, "end": v(187.2, -85) * mm, "construction": true});
            skLineSegment(sketch, "E26.3.1.5", {"start": v(-78.5, -87.5) * mm, "end": v(-91.5, -87.5) * mm});
            skLineSegment(sketch, "E26.6.1.5", {"start": v(-78.5, -82.5) * mm, "end": v(-91.5, -82.5) * mm});
            skPoint(sketch, "E26.9.1.5", {"position": v(-85, -85) * mm});
            skPoint(sketch, "E26.10.1.5", {"position": v(-91, -85) * mm});
            skLineSegment(sketch, "E26.11.1.5", {"start": v(-78.5, -87.5) * mm, "end": v(-78.5, -82.5) * mm});
            skLineSegment(sketch, "E26.14.1.5", {"start": v(-91.5, -87.5) * mm, "end": v(-91.5, -82.5) * mm});
            skLineSegment(sketch, "E26.0.2.5", {"start": v(-84.34, -85) * mm, "end": v(221.2, -85) * mm, "construction": true});
            skLineSegment(sketch, "E26.3.2.5", {"start": v(-44.5, -87.5) * mm, "end": v(-57.5, -87.5) * mm});
            skLineSegment(sketch, "E26.6.2.5", {"start": v(-44.5, -82.5) * mm, "end": v(-57.5, -82.5) * mm});
            skPoint(sketch, "E26.9.2.5", {"position": v(-51, -85) * mm});
            skPoint(sketch, "E26.10.2.5", {"position": v(-57, -85) * mm});
            skLineSegment(sketch, "E26.11.2.5", {"start": v(-44.5, -87.5) * mm, "end": v(-44.5, -82.5) * mm});
            skLineSegment(sketch, "E26.14.2.5", {"start": v(-57.5, -87.5) * mm, "end": v(-57.5, -82.5) * mm});
            skLineSegment(sketch, "E26.0.3.5", {"start": v(-50.34, -85) * mm, "end": v(255.2, -85) * mm, "construction": true});
            skLineSegment(sketch, "E26.3.3.5", {"start": v(-10.5, -87.5) * mm, "end": v(-23.5, -87.5) * mm});
            skLineSegment(sketch, "E26.6.3.5", {"start": v(-10.5, -82.5) * mm, "end": v(-23.5, -82.5) * mm});
            skPoint(sketch, "E26.9.3.5", {"position": v(-17, -85) * mm});
            skPoint(sketch, "E26.10.3.5", {"position": v(-23, -85) * mm});
            skLineSegment(sketch, "E26.11.3.5", {"start": v(-10.5, -87.5) * mm, "end": v(-10.5, -82.5) * mm});
            skLineSegment(sketch, "E26.14.3.5", {"start": v(-23.5, -87.5) * mm, "end": v(-23.5, -82.5) * mm});
            skLineSegment(sketch, "E26.0.4.5", {"start": v(-16.34, -85) * mm, "end": v(289.2, -85) * mm, "construction": true});
            skLineSegment(sketch, "E26.3.4.5", {"start": v(23.5, -87.5) * mm, "end": v(10.5, -87.5) * mm});
            skLineSegment(sketch, "E26.6.4.5", {"start": v(23.5, -82.5) * mm, "end": v(10.5, -82.5) * mm});
            skPoint(sketch, "E26.9.4.5", {"position": v(17, -85) * mm});
            skPoint(sketch, "E26.10.4.5", {"position": v(11, -85) * mm});
            skLineSegment(sketch, "E26.11.4.5", {"start": v(23.5, -87.5) * mm, "end": v(23.5, -82.5) * mm});
            skLineSegment(sketch, "E26.14.4.5", {"start": v(10.5, -87.5) * mm, "end": v(10.5, -82.5) * mm});
            skLineSegment(sketch, "E26.0.5.5", {"start": v(17.66, -85) * mm, "end": v(323.2, -85) * mm, "construction": true});
            skLineSegment(sketch, "E26.3.5.5", {"start": v(57.5, -87.5) * mm, "end": v(44.5, -87.5) * mm});
            skLineSegment(sketch, "E26.6.5.5", {"start": v(57.5, -82.5) * mm, "end": v(44.5, -82.5) * mm});
            skPoint(sketch, "E26.9.5.5", {"position": v(51, -85) * mm});
            skPoint(sketch, "E26.10.5.5", {"position": v(45, -85) * mm});
            skLineSegment(sketch, "E26.11.5.5", {"start": v(57.5, -87.5) * mm, "end": v(57.5, -82.5) * mm});
            skLineSegment(sketch, "E26.14.5.5", {"start": v(44.5, -87.5) * mm, "end": v(44.5, -82.5) * mm});
            skLineSegment(sketch, "E26.0.6.5", {"start": v(51.66, -85) * mm, "end": v(357.2, -85) * mm, "construction": true});
            skLineSegment(sketch, "E26.3.6.5", {"start": v(91.5, -87.5) * mm, "end": v(78.5, -87.5) * mm});
            skLineSegment(sketch, "E26.6.6.5", {"start": v(91.5, -82.5) * mm, "end": v(78.5, -82.5) * mm});
            skPoint(sketch, "E26.9.6.5", {"position": v(85, -85) * mm});
            skPoint(sketch, "E26.10.6.5", {"position": v(79, -85) * mm});
            skLineSegment(sketch, "E26.11.6.5", {"start": v(91.5, -87.5) * mm, "end": v(91.5, -82.5) * mm});
            skLineSegment(sketch, "E26.14.6.5", {"start": v(78.5, -87.5) * mm, "end": v(78.5, -82.5) * mm});
            skLineSegment(sketch, "E26.0.7.5", {"start": v(85.66, -85) * mm, "end": v(391.2, -85) * mm, "construction": true});
            skLineSegment(sketch, "E26.3.7.5", {"start": v(125.5, -87.5) * mm, "end": v(112.5, -87.5) * mm});
            skLineSegment(sketch, "E26.6.7.5", {"start": v(125.5, -82.5) * mm, "end": v(112.5, -82.5) * mm});
            skPoint(sketch, "E26.9.7.5", {"position": v(119, -85) * mm});
            skPoint(sketch, "E26.10.7.5", {"position": v(113, -85) * mm});
            skLineSegment(sketch, "E26.11.7.5", {"start": v(125.5, -87.5) * mm, "end": v(125.5, -82.5) * mm});
            skLineSegment(sketch, "E26.14.7.5", {"start": v(112.5, -87.5) * mm, "end": v(112.5, -82.5) * mm});
            skCircle(sketch, "E27.3.0.5", {"center": v(-119, -85) * mm, "radius": 1.5 * mm});
            skCircle(sketch, "E27.3.1.5", {"center": v(-85, -85) * mm, "radius": 1.5 * mm});
            skCircle(sketch, "E27.3.2.5", {"center": v(-51, -85) * mm, "radius": 1.5 * mm});
            skCircle(sketch, "E27.3.3.5", {"center": v(-17, -85) * mm, "radius": 1.5 * mm});
            skCircle(sketch, "E27.3.4.5", {"center": v(17, -85) * mm, "radius": 1.5 * mm});
            skCircle(sketch, "E27.3.5.5", {"center": v(51, -85) * mm, "radius": 1.5 * mm});
            skCircle(sketch, "E27.3.6.5", {"center": v(85, -85) * mm, "radius": 1.5 * mm});
            skCircle(sketch, "E27.3.7.5", {"center": v(119, -85) * mm, "radius": 1.5 * mm});
            skSolve(sketch);
        }
        {
            var Q0;
            Q0 = qSketchRegion(id + "F2", true);
            extrude(context, id + "F3", {"entities" : qUnion([Q0]), "operationType" : NewBodyOperationType.ADD, "depth" : 5 * mm, "offsetDistance" : 25 * mm});
        }
        {
            var Q0;
            Q0=makeQuery(id+"F2.imprint","IMPRINT",FACE,{"disambiguationData":[TD([[makeQuery(id+"F2.imprint","IMPRINT",EDGE,{"derivedFrom":sQuery(id+"F2.wireOp",EDGE,"E24")}),1.0]])]});
            var Q1;
            Q1=makeQuery(id+"F2.imprint","IMPRINT",FACE,{"disambiguationData":[TD([[makeQuery(id+"F2.imprint","IMPRINT",EDGE,{"derivedFrom":sQuery(id+"F2.wireOp",EDGE,"E25.1.0.1")}),1.0]])]});
            var Q2;
            Q2=makeQuery(id+"F2.imprint","IMPRINT",FACE,{"disambiguationData":[TD([[makeQuery(id+"F2.imprint","IMPRINT",EDGE,{"derivedFrom":sQuery(id+"F2.wireOp",EDGE,"E25.2.0.1")}),1.0]])]});
            var Q3;
            Q3=makeQuery(id+"F2.imprint","IMPRINT",FACE,{"disambiguationData":[TD([[makeQuery(id+"F2.imprint","IMPRINT",EDGE,{"derivedFrom":sQuery(id+"F2.wireOp",EDGE,"E25.3.0.1")}),1.0]])]});
            var Q4;
            Q4=makeQuery(id+"F2.imprint","IMPRINT",FACE,{"disambiguationData":[TD([[makeQuery(id+"F2.imprint","IMPRINT",EDGE,{"derivedFrom":sQuery(id+"F2.wireOp",EDGE,"E25.4.0.1")}),1.0]])]});
            var Q5;
            Q5=makeQuery(id+"F2.imprint","IMPRINT",FACE,{"disambiguationData":[TD([[makeQuery(id+"F2.imprint","IMPRINT",EDGE,{"derivedFrom":sQuery(id+"F2.wireOp",EDGE,"E25.4.1.1")}),1.0]])]});
            var Q6;
            Q6=makeQuery(id+"F2.imprint","IMPRINT",FACE,{"disambiguationData":[TD([[makeQuery(id+"F2.imprint","IMPRINT",EDGE,{"derivedFrom":sQuery(id+"F2.wireOp",EDGE,"E25.3.1.1")}),1.0]])]});
            var Q7;
            Q7=makeQuery(id+"F2.imprint","IMPRINT",FACE,{"disambiguationData":[TD([[makeQuery(id+"F2.imprint","IMPRINT",EDGE,{"derivedFrom":sQuery(id+"F2.wireOp",EDGE,"E25.2.1.1")}),1.0]])]});
            var Q8;
            Q8=makeQuery(id+"F2.imprint","IMPRINT",FACE,{"disambiguationData":[TD([[makeQuery(id+"F2.imprint","IMPRINT",EDGE,{"derivedFrom":sQuery(id+"F2.wireOp",EDGE,"E25.1.1.1")}),1.0]])]});
            var Q9;
            Q9=makeQuery(id+"F2.imprint","IMPRINT",FACE,{"disambiguationData":[TD([[makeQuery(id+"F2.imprint","IMPRINT",EDGE,{"derivedFrom":sQuery(id+"F2.wireOp",EDGE,"E25.0.1.1")}),1.0]])]});
            var Q10;
            Q10=makeQuery(id+"F2.imprint","IMPRINT",FACE,{"disambiguationData":[TD([[makeQuery(id+"F2.imprint","IMPRINT",EDGE,{"derivedFrom":sQuery(id+"F2.wireOp",EDGE,"E25.0.2.1")}),1.0]])]});
            var Q11;
            Q11=makeQuery(id+"F2.imprint","IMPRINT",FACE,{"disambiguationData":[TD([[makeQuery(id+"F2.imprint","IMPRINT",EDGE,{"derivedFrom":sQuery(id+"F2.wireOp",EDGE,"E25.1.2.1")}),1.0]])]});
            var Q12;
            Q12=makeQuery(id+"F2.imprint","IMPRINT",FACE,{"disambiguationData":[TD([[makeQuery(id+"F2.imprint","IMPRINT",EDGE,{"derivedFrom":sQuery(id+"F2.wireOp",EDGE,"E25.2.2.1")}),1.0]])]});
            var Q13;
            Q13=makeQuery(id+"F2.imprint","IMPRINT",FACE,{"disambiguationData":[TD([[makeQuery(id+"F2.imprint","IMPRINT",EDGE,{"derivedFrom":sQuery(id+"F2.wireOp",EDGE,"E25.3.2.1")}),1.0]])]});
            var Q14;
            Q14=makeQuery(id+"F2.imprint","IMPRINT",FACE,{"disambiguationData":[TD([[makeQuery(id+"F2.imprint","IMPRINT",EDGE,{"derivedFrom":sQuery(id+"F2.wireOp",EDGE,"E25.4.2.1")}),1.0]])]});
            var Q15;
            Q15=makeQuery(id+"F2.imprint","IMPRINT",FACE,{"disambiguationData":[TD([[makeQuery(id+"F2.imprint","IMPRINT",EDGE,{"derivedFrom":sQuery(id+"F2.wireOp",EDGE,"E25.5.2.1")}),1.0]])]});
            var Q16;
            Q16=makeQuery(id+"F2.imprint","IMPRINT",FACE,{"disambiguationData":[TD([[makeQuery(id+"F2.imprint","IMPRINT",EDGE,{"derivedFrom":sQuery(id+"F2.wireOp",EDGE,"E25.5.1.1")}),1.0]])]});
            var Q17;
            Q17=makeQuery(id+"F2.imprint","IMPRINT",FACE,{"disambiguationData":[TD([[makeQuery(id+"F2.imprint","IMPRINT",EDGE,{"derivedFrom":sQuery(id+"F2.wireOp",EDGE,"E25.5.0.1")}),1.0]])]});
            var Q18;
            Q18=makeQuery(id+"F2.imprint","IMPRINT",FACE,{"disambiguationData":[TD([[makeQuery(id+"F2.imprint","IMPRINT",EDGE,{"derivedFrom":sQuery(id+"F2.wireOp",EDGE,"E25.7.0.1")}),1.0]])]});
            var Q19;
            Q19=makeQuery(id+"F2.imprint","IMPRINT",FACE,{"disambiguationData":[TD([[makeQuery(id+"F2.imprint","IMPRINT",EDGE,{"derivedFrom":sQuery(id+"F2.wireOp",EDGE,"E25.6.0.1")}),1.0]])]});
            var Q20;
            Q20=makeQuery(id+"F2.imprint","IMPRINT",FACE,{"disambiguationData":[TD([[makeQuery(id+"F2.imprint","IMPRINT",EDGE,{"derivedFrom":sQuery(id+"F2.wireOp",EDGE,"E25.6.1.1")}),1.0]])]});
            var Q21;
            Q21=makeQuery(id+"F2.imprint","IMPRINT",FACE,{"disambiguationData":[TD([[makeQuery(id+"F2.imprint","IMPRINT",EDGE,{"derivedFrom":sQuery(id+"F2.wireOp",EDGE,"E25.7.1.1")}),1.0]])]});
            var Q22;
            Q22=makeQuery(id+"F2.imprint","IMPRINT",FACE,{"disambiguationData":[TD([[makeQuery(id+"F2.imprint","IMPRINT",EDGE,{"derivedFrom":sQuery(id+"F2.wireOp",EDGE,"E25.7.2.1")}),1.0]])]});
            var Q23;
            Q23=makeQuery(id+"F2.imprint","IMPRINT",FACE,{"disambiguationData":[TD([[makeQuery(id+"F2.imprint","IMPRINT",EDGE,{"derivedFrom":sQuery(id+"F2.wireOp",EDGE,"E25.6.2.1")}),1.0]])]});
            var Q24;
            Q24=makeQuery(id+"F2.imprint","IMPRINT",FACE,{"disambiguationData":[TD([[makeQuery(id+"F2.imprint","IMPRINT",EDGE,{"derivedFrom":sQuery(id+"F2.wireOp",EDGE,"E25.6.3.1")}),1.0]])]});
            var Q25;
            Q25=makeQuery(id+"F2.imprint","IMPRINT",FACE,{"disambiguationData":[TD([[makeQuery(id+"F2.imprint","IMPRINT",EDGE,{"derivedFrom":sQuery(id+"F2.wireOp",EDGE,"E25.7.3.1")}),1.0]])]});
            var Q26;
            Q26=makeQuery(id+"F2.imprint","IMPRINT",FACE,{"disambiguationData":[TD([[makeQuery(id+"F2.imprint","IMPRINT",EDGE,{"derivedFrom":sQuery(id+"F2.wireOp",EDGE,"E25.7.4.1")}),1.0]])]});
            var Q27;
            Q27=makeQuery(id+"F2.imprint","IMPRINT",FACE,{"disambiguationData":[TD([[makeQuery(id+"F2.imprint","IMPRINT",EDGE,{"derivedFrom":sQuery(id+"F2.wireOp",EDGE,"E25.6.4.1")}),1.0]])]});
            var Q28;
            Q28=makeQuery(id+"F2.imprint","IMPRINT",FACE,{"disambiguationData":[TD([[makeQuery(id+"F2.imprint","IMPRINT",EDGE,{"derivedFrom":sQuery(id+"F2.wireOp",EDGE,"E25.5.4.1")}),1.0]])]});
            var Q29;
            Q29=makeQuery(id+"F2.imprint","IMPRINT",FACE,{"disambiguationData":[TD([[makeQuery(id+"F2.imprint","IMPRINT",EDGE,{"derivedFrom":sQuery(id+"F2.wireOp",EDGE,"E25.5.3.1")}),1.0]])]});
            var Q30;
            Q30=makeQuery(id+"F2.imprint","IMPRINT",FACE,{"disambiguationData":[TD([[makeQuery(id+"F2.imprint","IMPRINT",EDGE,{"derivedFrom":sQuery(id+"F2.wireOp",EDGE,"E25.4.3.1")}),1.0]])]});
            var Q31;
            Q31=makeQuery(id+"F2.imprint","IMPRINT",FACE,{"disambiguationData":[TD([[makeQuery(id+"F2.imprint","IMPRINT",EDGE,{"derivedFrom":sQuery(id+"F2.wireOp",EDGE,"E25.4.4.1")}),1.0]])]});
            var Q32;
            Q32=makeQuery(id+"F2.imprint","IMPRINT",FACE,{"disambiguationData":[TD([[makeQuery(id+"F2.imprint","IMPRINT",EDGE,{"derivedFrom":sQuery(id+"F2.wireOp",EDGE,"E25.3.4.1")}),1.0]])]});
            var Q33;
            Q33=makeQuery(id+"F2.imprint","IMPRINT",FACE,{"disambiguationData":[TD([[makeQuery(id+"F2.imprint","IMPRINT",EDGE,{"derivedFrom":sQuery(id+"F2.wireOp",EDGE,"E25.3.3.1")}),1.0]])]});
            var Q34;
            Q34=makeQuery(id+"F2.imprint","IMPRINT",FACE,{"disambiguationData":[TD([[makeQuery(id+"F2.imprint","IMPRINT",EDGE,{"derivedFrom":sQuery(id+"F2.wireOp",EDGE,"E25.2.3.1")}),1.0]])]});
            var Q35;
            Q35=makeQuery(id+"F2.imprint","IMPRINT",FACE,{"disambiguationData":[TD([[makeQuery(id+"F2.imprint","IMPRINT",EDGE,{"derivedFrom":sQuery(id+"F2.wireOp",EDGE,"E25.2.4.1")}),1.0]])]});
            var Q36;
            Q36=makeQuery(id+"F2.imprint","IMPRINT",FACE,{"disambiguationData":[TD([[makeQuery(id+"F2.imprint","IMPRINT",EDGE,{"derivedFrom":sQuery(id+"F2.wireOp",EDGE,"E25.1.4.1")}),1.0]])]});
            var Q37;
            Q37=makeQuery(id+"F2.imprint","IMPRINT",FACE,{"disambiguationData":[TD([[makeQuery(id+"F2.imprint","IMPRINT",EDGE,{"derivedFrom":sQuery(id+"F2.wireOp",EDGE,"E25.1.3.1")}),1.0]])]});
            var Q38;
            Q38=makeQuery(id+"F2.imprint","IMPRINT",FACE,{"disambiguationData":[TD([[makeQuery(id+"F2.imprint","IMPRINT",EDGE,{"derivedFrom":sQuery(id+"F2.wireOp",EDGE,"E25.0.3.1")}),1.0]])]});
            var Q39;
            Q39=makeQuery(id+"F2.imprint","IMPRINT",FACE,{"disambiguationData":[TD([[makeQuery(id+"F2.imprint","IMPRINT",EDGE,{"derivedFrom":sQuery(id+"F2.wireOp",EDGE,"E25.0.4.1")}),1.0]])]});
            extrude(context, id + "F4", {"entities" : qUnion([Q0, Q1, Q2, Q3, Q4, Q5, Q6, Q7, Q8, Q9, Q10, Q11, Q12, Q13, Q14, Q15, Q16, Q17, Q18, Q19, Q20, Q21, Q22, Q23, Q24, Q25, Q26, Q27, Q28, Q29, Q30, Q31, Q32, Q33, Q34, Q35, Q36, Q37, Q38, Q39]), "operationType" : NewBodyOperationType.ADD, "oppositeDirection" : true, "depth" : 7.5 * mm, "offsetDistance" : 25 * mm, "hasSecondDirection" : true, "secondDirectionOppositeDirection" : false, "secondDirectionDepth" : 3.5 * mm});
        }
        {
            var Q0;
            Q0=makeQuery(id+"F1.opExtrude","CAP_FACE",FACE,{"disambiguationData":[OSD([sQuery(id+"F0.wireOp",EDGE,"E0.bottom"),sQuery(id+"F0.wireOp",EDGE,"E0.top"),sQuery(id+"F0.wireOp",EDGE,"E0.left"),sQuery(id+"F0.wireOp",EDGE,"E0.right"),sQuery(id+"F0.wireOp",EDGE,"E2"),sQuery(id+"F0.wireOp",EDGE,"E3"),sQuery(id+"F0.wireOp",EDGE,"E4"),sQuery(id+"F0.wireOp",EDGE,"E5"),sQuery(id+"F0.wireOp",EDGE,"E7.0.1.1"),sQuery(id+"F0.wireOp",EDGE,"E7.0.1.2"),sQuery(id+"F0.wireOp",EDGE,"E7.0.1.3"),sQuery(id+"F0.wireOp",EDGE,"E7.0.1.4"),sQuery(id+"F0.wireOp",EDGE,"E7.0.2.1"),sQuery(id+"F0.wireOp",EDGE,"E7.0.2.2"),sQuery(id+"F0.wireOp",EDGE,"E7.0.2.3"),sQuery(id+"F0.wireOp",EDGE,"E7.0.2.4"),sQuery(id+"F0.wireOp",EDGE,"E7.0.3.1"),sQuery(id+"F0.wireOp",EDGE,"E7.0.3.2"),sQuery(id+"F0.wireOp",EDGE,"E7.0.3.3"),sQuery(id+"F0.wireOp",EDGE,"E7.0.3.4"),sQuery(id+"F0.wireOp",EDGE,"E7.0.4.1"),sQuery(id+"F0.wireOp",EDGE,"E7.0.4.2"),sQuery(id+"F0.wireOp",EDGE,"E7.0.4.3"),sQuery(id+"F0.wireOp",EDGE,"E7.0.4.4"),sQuery(id+"F0.wireOp",EDGE,"E7.1.0.1"),sQuery(id+"F0.wireOp",EDGE,"E7.1.0.2"),sQuery(id+"F0.wireOp",EDGE,"E7.1.0.3"),sQuery(id+"F0.wireOp",EDGE,"E7.1.0.4"),sQuery(id+"F0.wireOp",EDGE,"E7.1.1.1"),sQuery(id+"F0.wireOp",EDGE,"E7.1.1.2"),sQuery(id+"F0.wireOp",EDGE,"E7.1.1.3"),sQuery(id+"F0.wireOp",EDGE,"E7.1.1.4"),sQuery(id+"F0.wireOp",EDGE,"E7.1.2.1"),sQuery(id+"F0.wireOp",EDGE,"E7.1.2.2"),sQuery(id+"F0.wireOp",EDGE,"E7.1.2.3"),sQuery(id+"F0.wireOp",EDGE,"E7.1.2.4"),sQuery(id+"F0.wireOp",EDGE,"E7.1.3.1"),sQuery(id+"F0.wireOp",EDGE,"E7.1.3.2"),sQuery(id+"F0.wireOp",EDGE,"E7.1.3.3"),sQuery(id+"F0.wireOp",EDGE,"E7.1.3.4"),sQuery(id+"F0.wireOp",EDGE,"E7.1.4.1"),sQuery(id+"F0.wireOp",EDGE,"E7.1.4.2"),sQuery(id+"F0.wireOp",EDGE,"E7.1.4.3"),sQuery(id+"F0.wireOp",EDGE,"E7.1.4.4"),sQuery(id+"F0.wireOp",EDGE,"E7.2.0.1"),sQuery(id+"F0.wireOp",EDGE,"E7.2.0.2"),sQuery(id+"F0.wireOp",EDGE,"E7.2.0.3"),sQuery(id+"F0.wireOp",EDGE,"E7.2.0.4"),sQuery(id+"F0.wireOp",EDGE,"E7.2.1.1"),sQuery(id+"F0.wireOp",EDGE,"E7.2.1.2"),sQuery(id+"F0.wireOp",EDGE,"E7.2.1.3"),sQuery(id+"F0.wireOp",EDGE,"E7.2.1.4"),sQuery(id+"F0.wireOp",EDGE,"E7.2.2.1"),sQuery(id+"F0.wireOp",EDGE,"E7.2.2.2"),sQuery(id+"F0.wireOp",EDGE,"E7.2.2.3"),sQuery(id+"F0.wireOp",EDGE,"E7.2.2.4"),sQuery(id+"F0.wireOp",EDGE,"E7.2.3.1"),sQuery(id+"F0.wireOp",EDGE,"E7.2.3.2"),sQuery(id+"F0.wireOp",EDGE,"E7.2.3.3"),sQuery(id+"F0.wireOp",EDGE,"E7.2.3.4"),sQuery(id+"F0.wireOp",EDGE,"E7.2.4.1"),sQuery(id+"F0.wireOp",EDGE,"E7.2.4.2"),sQuery(id+"F0.wireOp",EDGE,"E7.2.4.3"),sQuery(id+"F0.wireOp",EDGE,"E7.2.4.4"),sQuery(id+"F0.wireOp",EDGE,"E7.3.0.1"),sQuery(id+"F0.wireOp",EDGE,"E7.3.0.2"),sQuery(id+"F0.wireOp",EDGE,"E7.3.0.3"),sQuery(id+"F0.wireOp",EDGE,"E7.3.0.4"),sQuery(id+"F0.wireOp",EDGE,"E7.3.1.1"),sQuery(id+"F0.wireOp",EDGE,"E7.3.1.2"),sQuery(id+"F0.wireOp",EDGE,"E7.3.1.3"),sQuery(id+"F0.wireOp",EDGE,"E7.3.1.4"),sQuery(id+"F0.wireOp",EDGE,"E7.3.2.1"),sQuery(id+"F0.wireOp",EDGE,"E7.3.2.2"),sQuery(id+"F0.wireOp",EDGE,"E7.3.2.3"),sQuery(id+"F0.wireOp",EDGE,"E7.3.2.4"),sQuery(id+"F0.wireOp",EDGE,"E7.3.3.1"),sQuery(id+"F0.wireOp",EDGE,"E7.3.3.2"),sQuery(id+"F0.wireOp",EDGE,"E7.3.3.3"),sQuery(id+"F0.wireOp",EDGE,"E7.3.3.4"),sQuery(id+"F0.wireOp",EDGE,"E7.3.4.1"),sQuery(id+"F0.wireOp",EDGE,"E7.3.4.2"),sQuery(id+"F0.wireOp",EDGE,"E7.3.4.3"),sQuery(id+"F0.wireOp",EDGE,"E7.3.4.4"),sQuery(id+"F0.wireOp",EDGE,"E7.4.0.1"),sQuery(id+"F0.wireOp",EDGE,"E7.4.0.2"),sQuery(id+"F0.wireOp",EDGE,"E7.4.0.3"),sQuery(id+"F0.wireOp",EDGE,"E7.4.0.4"),sQuery(id+"F0.wireOp",EDGE,"E7.4.1.1"),sQuery(id+"F0.wireOp",EDGE,"E7.4.1.2"),sQuery(id+"F0.wireOp",EDGE,"E7.4.1.3"),sQuery(id+"F0.wireOp",EDGE,"E7.4.1.4"),sQuery(id+"F0.wireOp",EDGE,"E7.4.2.1"),sQuery(id+"F0.wireOp",EDGE,"E7.4.2.2"),sQuery(id+"F0.wireOp",EDGE,"E7.4.2.3"),sQuery(id+"F0.wireOp",EDGE,"E7.4.2.4"),sQuery(id+"F0.wireOp",EDGE,"E7.4.3.1"),sQuery(id+"F0.wireOp",EDGE,"E7.4.3.2"),sQuery(id+"F0.wireOp",EDGE,"E7.4.3.3"),sQuery(id+"F0.wireOp",EDGE,"E7.4.3.4"),sQuery(id+"F0.wireOp",EDGE,"E7.4.4.1"),sQuery(id+"F0.wireOp",EDGE,"E7.4.4.2"),sQuery(id+"F0.wireOp",EDGE,"E7.4.4.3"),sQuery(id+"F0.wireOp",EDGE,"E7.4.4.4"),sQuery(id+"F0.wireOp",EDGE,"E7.5.0.1"),sQuery(id+"F0.wireOp",EDGE,"E7.5.0.2"),sQuery(id+"F0.wireOp",EDGE,"E7.5.0.3"),sQuery(id+"F0.wireOp",EDGE,"E7.5.0.4"),sQuery(id+"F0.wireOp",EDGE,"E7.5.1.1"),sQuery(id+"F0.wireOp",EDGE,"E7.5.1.2"),sQuery(id+"F0.wireOp",EDGE,"E7.5.1.3"),sQuery(id+"F0.wireOp",EDGE,"E7.5.1.4"),sQuery(id+"F0.wireOp",EDGE,"E7.5.2.1"),sQuery(id+"F0.wireOp",EDGE,"E7.5.2.2"),sQuery(id+"F0.wireOp",EDGE,"E7.5.2.3"),sQuery(id+"F0.wireOp",EDGE,"E7.5.2.4"),sQuery(id+"F0.wireOp",EDGE,"E7.5.3.1"),sQuery(id+"F0.wireOp",EDGE,"E7.5.3.2"),sQuery(id+"F0.wireOp",EDGE,"E7.5.3.3"),sQuery(id+"F0.wireOp",EDGE,"E7.5.3.4"),sQuery(id+"F0.wireOp",EDGE,"E7.5.4.1"),sQuery(id+"F0.wireOp",EDGE,"E7.5.4.2"),sQuery(id+"F0.wireOp",EDGE,"E7.5.4.3"),sQuery(id+"F0.wireOp",EDGE,"E7.5.4.4"),sQuery(id+"F0.wireOp",EDGE,"E7.6.0.1"),sQuery(id+"F0.wireOp",EDGE,"E7.6.0.2"),sQuery(id+"F0.wireOp",EDGE,"E7.6.0.3"),sQuery(id+"F0.wireOp",EDGE,"E7.6.0.4"),sQuery(id+"F0.wireOp",EDGE,"E7.6.1.1"),sQuery(id+"F0.wireOp",EDGE,"E7.6.1.2"),sQuery(id+"F0.wireOp",EDGE,"E7.6.1.3"),sQuery(id+"F0.wireOp",EDGE,"E7.6.1.4"),sQuery(id+"F0.wireOp",EDGE,"E7.6.2.1"),sQuery(id+"F0.wireOp",EDGE,"E7.6.2.2"),sQuery(id+"F0.wireOp",EDGE,"E7.6.2.3"),sQuery(id+"F0.wireOp",EDGE,"E7.6.2.4"),sQuery(id+"F0.wireOp",EDGE,"E7.6.3.1"),sQuery(id+"F0.wireOp",EDGE,"E7.6.3.2"),sQuery(id+"F0.wireOp",EDGE,"E7.6.3.3"),sQuery(id+"F0.wireOp",EDGE,"E7.6.3.4"),sQuery(id+"F0.wireOp",EDGE,"E7.6.4.1"),sQuery(id+"F0.wireOp",EDGE,"E7.6.4.2"),sQuery(id+"F0.wireOp",EDGE,"E7.6.4.3"),sQuery(id+"F0.wireOp",EDGE,"E7.6.4.4"),sQuery(id+"F0.wireOp",EDGE,"E7.7.0.1"),sQuery(id+"F0.wireOp",EDGE,"E7.7.0.2"),sQuery(id+"F0.wireOp",EDGE,"E7.7.0.3"),sQuery(id+"F0.wireOp",EDGE,"E7.7.0.4"),sQuery(id+"F0.wireOp",EDGE,"E7.7.1.1"),sQuery(id+"F0.wireOp",EDGE,"E7.7.1.2"),sQuery(id+"F0.wireOp",EDGE,"E7.7.1.3"),sQuery(id+"F0.wireOp",EDGE,"E7.7.1.4"),sQuery(id+"F0.wireOp",EDGE,"E7.7.2.1"),sQuery(id+"F0.wireOp",EDGE,"E7.7.2.2"),sQuery(id+"F0.wireOp",EDGE,"E7.7.2.3"),sQuery(id+"F0.wireOp",EDGE,"E7.7.2.4"),sQuery(id+"F0.wireOp",EDGE,"E7.7.3.1"),sQuery(id+"F0.wireOp",EDGE,"E7.7.3.2"),sQuery(id+"F0.wireOp",EDGE,"E7.7.3.3"),sQuery(id+"F0.wireOp",EDGE,"E7.7.3.4"),sQuery(id+"F0.wireOp",EDGE,"E7.7.4.1"),sQuery(id+"F0.wireOp",EDGE,"E7.7.4.2"),sQuery(id+"F0.wireOp",EDGE,"E7.7.4.3"),sQuery(id+"F0.wireOp",EDGE,"E7.7.4.4")])],"isStart":false});
            var sketch = newSketch(context, id + "F5", { "sketchPlane" : qUnion([Q0])});
            skCircle(sketch, "E28", {"center": v(-133, 99) * mm, "radius": 2.55 * mm});
            skCircle(sketch, "E29.MirrorC", {"center": v(133, 99) * mm, "radius": 2.55 * mm});
            skCircle(sketch, "E30.MirrorC", {"center": v(133, -99) * mm, "radius": 2.55 * mm});
            skCircle(sketch, "E31.MirrorC", {"center": v(-133, -99) * mm, "radius": 2.55 * mm});
            skPoint(sketch, "E32.centerSnap0", {"position": v(-125, -17) * mm});
            skCircle(sketch, "E33", {"center": v(0, -99) * mm, "radius": 2.55 * mm});
            skCircle(sketch, "E34.MirrorC", {"center": v(0, 99) * mm, "radius": 2.55 * mm});
            skCircle(sketch, "E35", {"center": v(-133, 0) * mm, "radius": 2.55 * mm});
            skCircle(sketch, "E36.MirrorC", {"center": v(133, 0) * mm, "radius": 2.55 * mm});
            skSolve(sketch);
        }
        {
            var Q0;
            Q0 = qSketchRegion(id + "F5", true);
            extrude(context, id + "F6", {"entities" : qUnion([Q0]), "operationType" : NewBodyOperationType.REMOVE, "oppositeDirection" : true, "depth" : 5 * mm, "offsetDistance" : 25 * mm});
        }
        {
            var Q0;
            Q0=makeQuery(id+"F0.imprint","IMPRINT",FACE,{"disambiguationData":[TD([[makeQuery(id+"F0.imprint","IMPRINT",EDGE,{"derivedFrom":sQuery(id+"F0.wireOp",EDGE,"E9.MirrorCS")}),1.0]])]});
            extrude(context, id + "F7", {"entities" : qUnion([Q0]), "depth" : 6 * mm, "offsetDistance" : 25 * mm});
        }
        {
            var Q0;
            Q0=makeQuery(id+"F0.imprint","IMPRINT",FACE,{"disambiguationData":[TD([[makeQuery(id+"F0.imprint","IMPRINT",EDGE,{"derivedFrom":sQuery(id+"F0.wireOp",EDGE,"E14.MirrorCS")}),-1.0]])]});
            var Q1;
            {var subQ0=sQuery(id+"F0.wireOp",EDGE,"E19");Q1=makeQuery(id+"F0.imprint","IMPRINT",FACE,{"disambiguationData":[TD([[makeQuery(id+"F0.imprint","IMPRINT",EDGE,{"derivedFrom":subQ0}),1.0]])]});}
            var Q2;
            {var subQ0=sQuery(id+"F0.wireOp",EDGE,"E20");Q2=makeQuery(id+"F0.imprint","IMPRINT",FACE,{"disambiguationData":[TD([[makeQuery(id+"F0.imprint","IMPRINT",EDGE,{"derivedFrom":subQ0}),-1.0]])]});}
            extrude(context, id + "F8", {"entities" : qUnion([Q0, Q1, Q2]), "depth" : 5 * mm, "offsetDistance" : 25 * mm});
        }
    });
